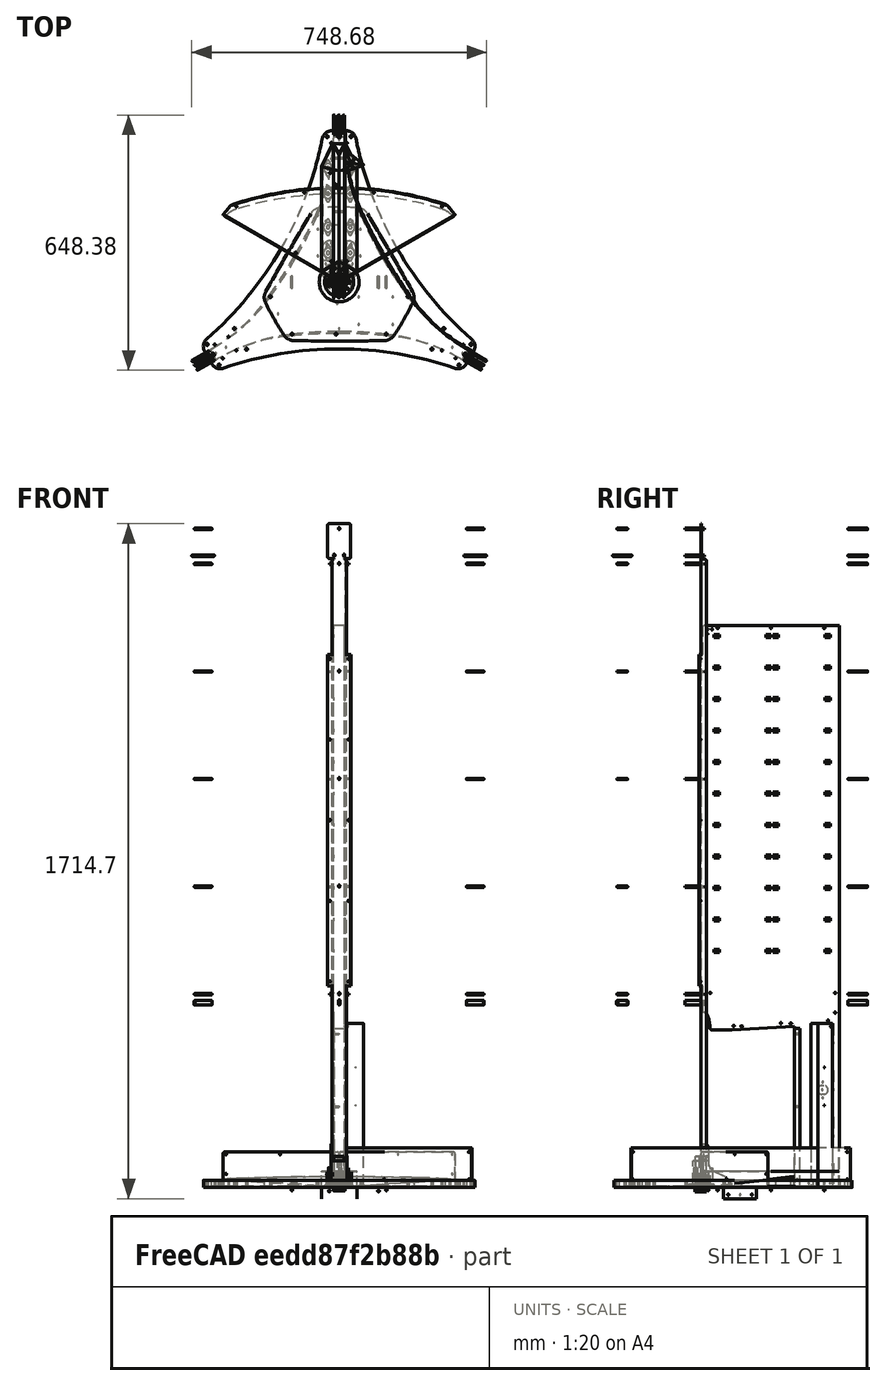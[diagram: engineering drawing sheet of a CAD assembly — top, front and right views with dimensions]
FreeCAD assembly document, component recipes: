
FREECAD ASSEMBLY — COMPONENT RECIPES ("composit_full_size3")

This assembly document has 76 components, labeled P0..P75 below (a component is one placed body or linked part). 73 of them carry a construction recipe — the FreeCAD feature program that regenerates the part from scratch, quoted from this document or its linked companion documents; the rest are supplied as boundary geometry only. No exploded tour is included for this assembly.
NOTE — this tour is split across 3 documents so each fits a 32k-token context. This is document 1: the component sections continue in the remaining 2 documents, each repeating the header above.
COMPONENT P0 — recipe-attached ("tech_sector_pillar_material_0.30ansi", modeled in this document).
Construction recipe (the document's own serialized feature program — sketch geometry with constraints, then the solid features built on it; lengths are millimeters unless a unit is written):

FEATURE [Sketcher::SketchObject] Sketch062
  ArcFitTolerance = 0
  AttachmentSupport = -> [XY_Plane036]
  FullyConstrained = true
  MakeInternals = false
  MapMode = 5
  expr: Constraints[3] = <<Properties>>.endface_width / 2 + 0.5 mm
  sketch-geometry (7):
    g0: LineSegment StartX=61.9452 StartY=297.209 StartZ=0 EndX=15 EndY=280 EndZ=0
    g1: LineSegment StartX=15 StartY=280 StartZ=0 EndX=15 EndY=335 EndZ=0
    g2: LineSegment StartX=15 StartY=335 StartZ=0 EndX=62.031 EndY=297.743 EndZ=0
    g3: LineSegment [constr] StartX=61.9452 StartY=297.209 StartZ=0 EndX=62.4647 EndY=297.399 EndZ=0
    g4: LineSegment [constr] StartX=62.4647 StartY=297.399 StartZ=0 EndX=62.031 EndY=297.743 EndZ=0
    g5: LineSegment [constr] StartX=61.9452 StartY=297.209 StartZ=0 EndX=61.8385 EndY=297.5 EndZ=0
    g6: LineSegment [constr] StartX=61.8385 StartY=297.5 StartZ=0 EndX=62.031 EndY=297.743 EndZ=0
  constraints (20):
    c: Coincident(g0,g1)
    c: Vertical(g1)
    c: Coincident(g1,g2)
    c: DistanceX(g1) = 15
    c: Distance(g1) = 55
    c: Distance(g2) = 60
    c: Distance(g0) = 50
    c: Coincident(g3,g0)
    c: Coincident(g4,g3)
    c: Coincident(g4,g2)
    c: Parallel(g0,g3)
    c: Parallel(g4,g2)
    c: Equal(g3,g4)
    c: Coincident(g0,g5)
    c: Coincident(g5,g6)
    c: Coincident(g6,g2)
    c: Perpendicular(g3,g5)
    c: Perpendicular(g4,g6)
    c: Distance(g5) = 0.31
    c: DistanceY(g1) = 335
FEATURE [PartDesign::FeaturePython] BaseBend020  # WARN: FeaturePython — macro-defined, semantics opaque (R4)
  BendSide = 0
  BendSketch = -> Sketch062
  MidPlane = false
  Reverse = false
  Suppressed = false
  length = 413
  radius = 0.1
  thickness = 0.3
  expr: radius = composit_properties#<<Properties>>.bend_r
  expr: thickness = composit_properties#<<Properties>>.al_thickness
FEATURE [PartDesign::FeaturePython] Bend009  # WARN: FeaturePython — macro-defined, semantics opaque (R4)
  AutoMiter = true
  BaseFeature = -> BaseBend020
  BendType = 0
  LengthList = [15]
  LengthSpec = 0
  NonperforationMaxLength = 5
  Perforate = false
  PerforationAngle = 0
  PerforationInitialLength = 5
  PerforationMaxLength = 5
  ReliefFactor = 0.7
  Suppressed = false
  UseReliefFactor = false
  angle = 90
  baseObject = -> BaseBend020 [Edge17,Edge4,Edge33,Edge32,Edge16,Edge3]
  bendAList = [90]
  extend1 = 0
  extend2 = 0
  gap1 = 0
  gap2 = 0
  invert = true
  kfactor = 0.5
  length = 15
  maxExtendDist = 5
  minGap = 0.1
  minReliefGap = 1
  miterangle1 = 0
  miterangle2 = 0
  offset = 0
  radius = 0.1
  reliefType = 0
  reliefd = 1
  reliefw = 0.8
  sketchflip = false
  sketchinvert = false
  unfold = false
  expr: radius = BaseBend020.radius
FEATURE [Sketcher::SketchObject] Sketch075
  ArcFitTolerance = 0
  AttachmentSupport = -> [XY_Plane036]
  ExternalGeometry = -> [Sketch062]
  FullyConstrained = true
  MakeInternals = false
  MapMode = 5
  expr: Constraints[34] = <<Properties>>.rivet_d
  sketch-geometry (14):
    g0: LineSegment [constr] StartX=15 StartY=280 StartZ=0 EndX=62.4647 EndY=297.399 EndZ=0
    g1: LineSegment [constr] StartX=62.4647 StartY=297.399 StartZ=0 EndX=15 EndY=335 EndZ=0
    g2: LineSegment [constr] StartX=15 StartY=280 StartZ=0 EndX=30.7162 EndY=302.5 EndZ=0
    g3: LineSegment [constr] StartX=30.7162 StartY=302.5 StartZ=0 EndX=15 EndY=335 EndZ=0
    g4: LineSegment [constr] StartX=30.7162 StartY=302.5 StartZ=0 EndX=62.4647 EndY=297.399 EndZ=0
    g5: LineSegment [constr] StartX=15 StartY=302.5 StartZ=0 EndX=30.7162 EndY=302.5 EndZ=0
    g6: LineSegment [constr] StartX=30.7162 StartY=302.5 StartZ=0 EndX=36.1253 EndY=287.744 EndZ=0
    g7: LineSegment [constr] StartX=30.7162 StartY=302.5 StartZ=0 EndX=40.4751 EndY=314.819 EndZ=0
    g8: Circle CenterX=34.4044 CenterY=292.439 CenterZ=0 NormalX=0 NormalY=0 NormalZ=1 AngleXU=0 Radius=1.7
    g9: Circle CenterX=36.2097 CenterY=309.435 CenterZ=0 NormalX=0 NormalY=0 NormalZ=1 AngleXU=0 Radius=1.7
    g10: Circle CenterX=20.588 CenterY=302.5 CenterZ=0 NormalX=0 NormalY=0 NormalZ=1 AngleXU=0 Radius=1.7
    g11: LineSegment [constr] StartX=20.588 StartY=302.5 StartZ=0 EndX=36.2097 EndY=309.435 EndZ=0
    g12: LineSegment [constr] StartX=36.2097 StartY=309.435 StartZ=0 EndX=34.4044 EndY=292.439 EndZ=0
    g13: LineSegment [constr] StartX=34.4044 StartY=292.439 StartZ=0 EndX=20.588 EndY=302.5 EndZ=0
  constraints (36):
    c: Coincident(g-4,g0)
    c: Coincident(g0,g1)
    c: Coincident(g1,g-3)
    c: PointOnObject(g-4,g0)
    c: PointOnObject(g-3,g1)
    c: Coincident(g0,g2)
    c: Coincident(g2,g3)
    c: Coincident(g2,g4)
    c: Coincident(g4,g0)
    c: Coincident(g3,g1)
    c: Coincident(g5,g2)
    c: Horizontal(g5)
    c: Coincident(g5,g6)
    c: PointOnObject(g6,g0)
    c: Perpendicular(g0,g6)
    c: Vertical(g5,g0)
    c: Equal(g6,g5)
    c: Coincident(g7,g2)
    c: PointOnObject(g7,g1)
    c: Perpendicular(g1,g7)
    c: Equal(g6,g7)
    c: PointOnObject(g8,g6)
    c: PointOnObject(g9,g7)
    c: PointOnObject(g10,g5)
    c: Coincident(g11,g10)
    c: Coincident(g11,g9)
    c: Coincident(g11,g12)
    c: Coincident(g12,g8)
    c: Coincident(g12,g13)
    c: Coincident(g13,g11)
    c: Equal(g13,g11)
    c: Equal(g11,g12)
    c: Equal(g8,g10)
    c: Equal(g8,g9)
    c: Diameter(g8) = 3.4
    c: Distance(g8,g6) = 5
FEATURE [PartDesign::Pocket] Pocket035
  BaseFeature = -> Bend009
  Direction = (0,0,-1)
  Length = 5
  Length2 = 5
  Midplane = true
  Profile = -> Sketch075
  ReferenceAxis = -> Sketch075 [N_Axis]
  Suppressed = false
  Type = 1
FEATURE [PartDesign::Plane] DatumPlane001
  AttachmentOffset = pos=(0,0,0) rot=(0,1,0;1.5708rad)
  AttachmentSupport = -> [Sketch062]
  Length = 362.992
  MapMode = 7
  Placement = pos=(15,335,0) rot=(-0.89718,0.312304,0.312304;4.6041rad)
  ResizeMode = 0
  Width = 509.896
FEATURE [Sketcher::SketchObject] Sketch077
  ArcFitTolerance = 0
  AttachmentSupport = -> [DatumPlane001]
  FullyConstrained = true
  MakeInternals = false
  MapMode = 5
  Placement = pos=(15,335,0) rot=(0.89718,-0.312304,-0.312304;1.67908rad)
  expr: Constraints[1] = <<Properties>>.rivet_d
  expr: Constraints[3] = BaseBend020.length
  sketch-geometry (4):
    g0: Circle CenterX=10 CenterY=7 CenterZ=0 NormalX=0 NormalY=0 NormalZ=1 AngleXU=0 Radius=1.7
    g1: Circle CenterX=10 CenterY=406 CenterZ=0 NormalX=0 NormalY=0 NormalZ=1 AngleXU=0 Radius=1.7
    g2: GeomPoint [constr] X=0 Y=413 Z=0
    g3: LineSegment [constr] StartX=0 StartY=206.5 StartZ=0 EndX=10 EndY=206.5 EndZ=0
  constraints (10):
    c: Equal(g0,g1)
    c: Diameter(g0) = 3.4
    c: PointOnObject(g2,g-2)
    c: DistanceY(g2) = 413
    c: DistanceX(g0) = 10
    c: DistanceY(g0) = 7
    c: Vertical(g1,g0)
    c: Horizontal(g3)
    c: Symmetric(g-1,g2,g3)
    c: Symmetric(g1,g0,g3)
FEATURE [PartDesign::Hole] Hole006
  BaseFeature = -> Pocket035
  CustomThreadClearance = 0
  Depth = 1
  DepthType = 0
  Diameter = 3.4
  DrillForDepth = false
  DrillPoint = 1
  DrillPointAngle = 118
  HoleCutCountersinkAngle = 90
  HoleCutCustomValues = false
  HoleCutDepth = 0
  HoleCutDiameter = 6.1
  HoleCutType = 0
  ModelThread = false
  Profile = -> Sketch077
  Reversed = true
  Suppressed = false
  Tapered = false
  TaperedAngle = 90
  ThreadClass = 0
  ThreadDepth = 1
  ThreadDepthType = 0
  ThreadDirection = 0
  ThreadFit = 0
  ThreadSize = 0
  ThreadType = 0
  Threaded = false
  UseCustomThreadClearance = false
  expr: Diameter = <<Properties>>.rivet_d
FEATURE [Sketcher::SketchObject] Sketch078  label="pillar_magnet_fix"
  ArcFitTolerance = 0
  AttachmentOffset = pos=(0,0,0) rot=(0,1,0;1.5708rad)
  AttachmentSupport = -> [Sketch062]
  FullyConstrained = true
  MakeInternals = false
  MapMode = 7
  Placement = pos=(15,280,0) rot=(0.57735,0.57735,0.57735;2.0944rad)
  expr: Constraints[11] = <<Properties>>.rivet_d
  sketch-geometry (8):
    g0: ArcOfCircle CenterX=32.5 CenterY=244.5 CenterZ=0 NormalX=0 NormalY=0 NormalZ=1 AngleXU=0 Radius=11 StartAngle=4.71239 EndAngle=7.85398
    g1: ArcOfCircle CenterX=27.5 CenterY=244.5 CenterZ=0 NormalX=0 NormalY=0 NormalZ=1 AngleXU=0 Radius=11 StartAngle=1.5708 EndAngle=4.71239
    g2: LineSegment StartX=32.5 StartY=255.5 StartZ=0 EndX=27.5 EndY=255.5 EndZ=0
    g3: LineSegment StartX=27.5 StartY=233.5 StartZ=0 EndX=32.5 EndY=233.5 EndZ=0
    g4: Circle CenterX=30 CenterY=224.5 CenterZ=0 NormalX=0 NormalY=0 NormalZ=1 AngleXU=0 Radius=1.7
    g5: Circle CenterX=30 CenterY=264.5 CenterZ=0 NormalX=0 NormalY=0 NormalZ=1 AngleXU=0 Radius=1.7
    g6: LineSegment [constr] StartX=27.5 StartY=244.5 StartZ=0 EndX=30 EndY=244.5 EndZ=0
    g7: LineSegment [constr] StartX=32.5 StartY=244.5 StartZ=0 EndX=30 EndY=244.5 EndZ=0
  constraints (20):
    c: Tangent(g0,g2) = -1.5708
    c: Tangent(g2,g1) = -1.5708
    c: Tangent(g1,g3) = -1.5708
    c: Tangent(g3,g0) = -1.5708
    c: Equal(g0,g1)
    c: Coincident(g6,g1)
    c: Coincident(g7,g0)
    c: Coincident(g7,g6)
    c: Equal(g6,g7)
    c: Symmetric(g4,g5,g6)
    c: Equal(g4,g5)
    c: Diameter(g4) = 3.4
    c: Parallel(g6,g7)
    c: Distance(g1,g0) = 5
    c: Diameter(g0) = 22
    c: Horizontal(g1,g0)
    c: DistanceY(g4,g5) = 40
    c: DistanceY(g6) = 244.5  'height'
    c: DistanceX(g6) = 30
    c: Vertical(g4,g5)
FEATURE [PartDesign::Pocket] Pocket037
  BaseFeature = -> Hole006
  Direction = (-1,2e-16,0)
  Length = 5
  Length2 = 5
  Midplane = true
  Profile = -> Sketch078
  ReferenceAxis = -> Sketch078 [N_Axis]
  Suppressed = false
  Type = 0
FEATURE [Sketcher::SketchObject] Sketch079
  ArcFitTolerance = 0
  AttachmentSupport = -> [DatumPlane001]
  FullyConstrained = true
  MakeInternals = false
  MapMode = 5
  Placement = pos=(15,335,0) rot=(0.89718,-0.312304,-0.312304;1.67908rad)
  expr: Constraints[3] = BaseBend020.length - 111.35 mm
  sketch-geometry (2):
    g0: Circle CenterX=35 CenterY=301.65 CenterZ=0 NormalX=0 NormalY=0 NormalZ=1 AngleXU=0 Radius=1.25
    g1: Circle CenterX=35 CenterY=205.65 CenterZ=0 NormalX=0 NormalY=0 NormalZ=1 AngleXU=0 Radius=1.25
  constraints (6):
    c: Vertical(g1,g0)
    c: DistanceY(g1,g0) = 96
    c: DistanceX(g1) = 35
    c: DistanceY(g0) = 301.65
    c: Equal(g1,g0)
    c: Diameter(g1) = 2.5
FEATURE [PartDesign::Hole] Hole009
  BaseFeature = -> Pocket037
  CustomThreadClearance = 0
  Depth = 25
  DepthType = 0
  Diameter = 2.5
  DrillForDepth = false
  DrillPoint = 1
  DrillPointAngle = 118
  HoleCutCountersinkAngle = 90
  HoleCutCustomValues = false
  HoleCutDepth = 0
  HoleCutDiameter = 6.1
  HoleCutType = 0
  ModelThread = false
  Profile = -> Sketch079
  Reversed = true
  Suppressed = false
  Tapered = false
  TaperedAngle = 90
  ThreadClass = 0
  ThreadDepth = 25
  ThreadDepthType = 0
  ThreadDirection = 0
  ThreadFit = 0
  ThreadSize = 0
  ThreadType = 0
  Threaded = false
  UseCustomThreadClearance = false
FEATURE [PartDesign::Body] Body073  label="tech_sector_pillar_material_0.30ansi"
  AllowCompound = false
  Group = -> [Sketch062,BaseBend020,Bend009,Sketch075,Pocket035,DatumPlane001,Sketch077,Hole006,Sketch078,Pocket037,Sketch079,Hole009]
  Origin = -> Origin036
  Placement = pos=(0,0,3) rot=(0,0,1;0rad)
  Tip = -> Hole009
COMPONENT P1 — recipe-attached ("tech_sector_hor", modeled in this document).
Construction recipe (the document's own serialized feature program — sketch geometry with constraints, then the solid features built on it; lengths are millimeters unless a unit is written):

FEATURE [PartDesign::SubShapeBinder] Binder038
  BindCopyOnChange = 0
  BindMode = 0
  ClaimChildren = true
  Context = -> Body074 [Binder038.]
  Fuse = false
  MakeFace = true
  OffsetFill = false
  OffsetIntersection = false
  OffsetJoinType = 0
  OffsetOpenResult = false
  PartialLoad = false
  Relative = true
  Support = -> [Compound037]
  _Version = 2
FEATURE [PartDesign::Pad] Pad008
  Direction = (0,0,1)
  Length = 3
  Length2 = 10
  Profile = -> Binder038
  Suppressed = false
  Type = 0
FEATURE [PartDesign::SubShapeBinder] Binder044
  BindCopyOnChange = 0
  BindMode = 0
  ClaimChildren = false
  Context = -> Body074 [Binder044.]
  Fuse = false
  MakeFace = true
  OffsetFill = false
  OffsetIntersection = false
  OffsetJoinType = 0
  OffsetOpenResult = false
  PartialLoad = false
  Relative = true
  Support = -> [Body073[Pocket035.Sketch075.]]
  _Version = 2
FEATURE [PartDesign::Pocket] Pocket036
  BaseFeature = -> Pad008
  Direction = (0,0,-1)
  Length = 5
  Length2 = 5
  Midplane = true
  Profile = -> Binder044
  Suppressed = false
  Type = 1
FEATURE [PartDesign::Plane] DatumPlane
  AttachmentOffset = pos=(0,0,0) rot=(0,1,0;0.523599rad)
  AttachmentSupport = -> [XZ_Plane037]
  Length = 552.693
  MapMode = 5
  Placement = pos=(0,0,0) rot=(0.935113,0.250563,0.250563;1.63783rad)
  ResizeMode = 0
  Width = 82.2624
FEATURE [PartDesign::Mirrored] Mirrored003
  BaseFeature = -> Pocket036
  MirrorPlane = -> DatumPlane
  Originals = -> [Pocket036]
  Suppressed = false
  TransformMode = 0
FEATURE [Sketcher::SketchObject] Sketch083
  ArcFitTolerance = 0
  AttachmentSupport = -> [XY_Plane037]
  ExternalGeometry = -> [Binder038]
  FullyConstrained = true
  MakeInternals = false
  MapMode = 5
  expr: Constraints[4] = <<Properties>>.rivet_d
  sketch-geometry (2):
    g0: LineSegment [constr] StartX=212.95 StartY=122.947 StartZ=0 EndX=201.691 EndY=116.447 EndZ=0
    g1: Circle CenterX=201.691 CenterY=116.447 CenterZ=0 NormalX=0 NormalY=0 NormalZ=1 AngleXU=0 Radius=1.7
  constraints (5):
    c: Coincident(g0,g-3)
    c: Perpendicular(g-3,g0)
    c: Distance(g0) = 13
    c: Coincident(g1,g0)
    c: Diameter(g1) = 3.4
FEATURE [PartDesign::Hole] Hole011
  BaseFeature = -> Mirrored003
  CustomThreadClearance = 0
  Depth = 25
  DepthType = 0
  Diameter = 3.4
  DrillForDepth = false
  DrillPoint = 1
  DrillPointAngle = 118
  HoleCutCountersinkAngle = 90
  HoleCutCustomValues = false
  HoleCutDepth = 0
  HoleCutDiameter = 6.1
  HoleCutType = 0
  ModelThread = false
  Profile = -> Sketch083
  Reversed = true
  Suppressed = false
  Tapered = false
  TaperedAngle = 90
  ThreadClass = 0
  ThreadDepth = 25
  ThreadDepthType = 0
  ThreadDirection = 0
  ThreadFit = 0
  ThreadSize = 0
  ThreadType = 0
  Threaded = false
  UseCustomThreadClearance = false
  expr: Diameter = <<Properties>>.rivet_d
FEATURE [PartDesign::Body] Body074  label="tech_sector_hor"
  AllowCompound = false
  Group = -> [Binder038,Pad008,Binder044,Pocket036,DatumPlane,Mirrored003,Sketch083,Hole011]
  Origin = -> Origin037
  Tip = -> Hole011
COMPONENT P2 — recipe-attached ("tech_sector_plexiglass_material_0.30ansi", modeled in this document).
Construction recipe (the document's own serialized feature program — sketch geometry with constraints, then the solid features built on it; lengths are millimeters unless a unit is written):

FEATURE [PartDesign::SubShapeBinder] Binder045
  BindCopyOnChange = 0
  BindMode = 0
  ClaimChildren = false
  Context = -> Body077 [Binder045.]
  Fuse = false
  MakeFace = true
  OffsetFill = false
  OffsetIntersection = false
  OffsetJoinType = 0
  OffsetOpenResult = false
  PartialLoad = false
  Relative = true
  Support = -> [Body074[Binder038.Compound037.Sketch063.]]
  _Version = 2
FEATURE [Sketcher::SketchObject] Sketch076
  ArcFitTolerance = 0
  AttachmentSupport = -> [XY_Plane041]
  ExternalGeometry = -> [Binder045]
  FullyConstrained = true
  MakeInternals = false
  MapMode = 5
  sketch-geometry (5):
    g0: LineSegment StartX=15 StartY=335 StartZ=0 EndX=62.031 EndY=297.743 EndZ=0
    g1: ArcOfCircle CenterX=-320.353 CenterY=-184.956 CenterZ=0 NormalX=0 NormalY=0 NormalZ=1 AngleXU=0 Radius=615.805 StartAngle=0.146355 EndAngle=0.900842
    g2: LineSegment StartX=288.868 StartY=-95.1511 StartZ=0 EndX=297.619 EndY=-154.51 EndZ=0
    g3: LineSegment [constr] StartX=-320.353 StartY=-184.956 StartZ=0 EndX=212.95 EndY=122.947 EndZ=0
    g4: LineSegment [constr] StartX=62.031 StartY=297.743 StartZ=0 EndX=288.868 EndY=-95.1511 EndZ=0
  constraints (12):
    c: Coincident(g0,g-4)
    c: Coincident(g1,g-4)
    c: Coincident(g1,g0)
    c: Tangent(g2,g1) = 1.5708
    c: Coincident(g3,g1)
    c: Coincident(g3,g-4)
    c: Vertical(g0,g-5)
    c: Equal(g0,g2)
    c: PointOnObject(g-3,g0)
    c: Coincident(g4,g0)
    c: Coincident(g4,g1)
    c: Perpendicular(g3,g4)
FEATURE [PartDesign::FeaturePython] BaseBend021  # WARN: FeaturePython — macro-defined, semantics opaque (R4)
  BendSide = 1
  BendSketch = -> Sketch076
  MidPlane = false
  Reverse = false
  Suppressed = false
  length = 419
  radius = 1
  thickness = 1.5
  expr: length = BaseBend020.length + composit_properties#<<Properties>>.thickness * 2
FEATURE [PartDesign::Fillet] Fillet
  Base = -> BaseBend021 [Edge10,Edge8,Edge25,Edge23]
  BaseFeature = -> BaseBend021
  Radius = 3
  SupportTransform = false
  Suppressed = false
  UseAllEdges = false
FEATURE [PartDesign::SubShapeBinder] Binder046
  BindCopyOnChange = 0
  BindMode = 0
  ClaimChildren = false
  Context = -> Body077 [Binder046.]
  Fuse = false
  MakeFace = true
  OffsetFill = false
  OffsetIntersection = false
  OffsetJoinType = 0
  OffsetOpenResult = false
  PartialLoad = false
  Relative = true
  Support = -> [Body073[Hole006.Sketch077.]]
  _Version = 2
FEATURE [PartDesign::SubShapeBinder] Binder047
  BindCopyOnChange = 0
  BindMode = 0
  ClaimChildren = true
  Context = -> Body077 [Binder047.]
  Fuse = false
  MakeFace = true
  OffsetFill = false
  OffsetIntersection = false
  OffsetJoinType = 0
  OffsetOpenResult = false
  PartialLoad = false
  Relative = true
  Support = -> [Body073[Sketch079.]]
  _Version = 2
FEATURE [PartDesign::Plane] DatumPlane002
  AttachmentOffset = pos=(0,0,0) rot=(0,1,0;0.523599rad)
  AttachmentSupport = -> [XZ_Plane041]
  Length = 622.679
  MapMode = 5
  Placement = pos=(0,0,0) rot=(0.935113,0.250563,0.250563;1.63783rad)
  ResizeMode = 0
  Width = 540.655
FEATURE [Sketcher::SketchObject] Sketch084
  ArcFitTolerance = 0
  AttachmentSupport = -> [Binder046]
  ExternalGeometry = -> [Binder046]
  FullyConstrained = false
  MakeInternals = false
  MapMode = 5
  Placement = pos=(168.839,213.132,5.5e-14) rot=(0.239007,0.686613,0.686613;2.67238rad)
  sketch-geometry (3):
    g0: Circle CenterX=186.261 CenterY=409.25 CenterZ=0 NormalX=0 NormalY=0 NormalZ=1 AngleXU=0 Radius=1.69397
    g1: Circle CenterX=186.261 CenterY=9.75 CenterZ=0 NormalX=0 NormalY=0 NormalZ=1 AngleXU=0 Radius=1.72481
    g2: GeomPoint [constr] X=186.261 Y=209.5 Z=0
  constraints (4):
    c: Symmetric(g-4,g-3,g2)
    c: Symmetric(g1,g0,g2)
    c: Vertical(g-3,g0)
    c: DistanceY(g-3,g0) = 0.25
FEATURE [PartDesign::Hole] Hole007
  BaseFeature = -> Fillet
  CustomThreadClearance = 0
  Depth = 25
  DepthType = 0
  Diameter = 3.4
  DrillForDepth = false
  DrillPoint = 1
  DrillPointAngle = 118
  HoleCutCountersinkAngle = 90
  HoleCutCustomValues = false
  HoleCutDepth = 0
  HoleCutDiameter = 6.1
  HoleCutType = 0
  ModelThread = false
  Profile = -> Sketch084
  Reversed = true
  Suppressed = false
  Tapered = false
  TaperedAngle = 90
  ThreadClass = 0
  ThreadDepth = 25
  ThreadDepthType = 0
  ThreadDirection = 0
  ThreadFit = 0
  ThreadSize = 0
  ThreadType = 0
  Threaded = false
  UseCustomThreadClearance = false
  expr: Diameter = <<Properties>>.rivet_d
FEATURE [PartDesign::Hole] Hole008
  BaseFeature = -> Hole007
  CustomThreadClearance = 0
  Depth = 25
  DepthType = 0
  Diameter = 3.4
  DrillForDepth = false
  DrillPoint = 1
  DrillPointAngle = 118
  HoleCutCountersinkAngle = 90
  HoleCutCustomValues = false
  HoleCutDepth = 0
  HoleCutDiameter = 6.1
  HoleCutType = 0
  ModelThread = false
  Profile = -> Binder047
  Reversed = true
  Suppressed = false
  Tapered = false
  TaperedAngle = 90
  ThreadClass = 0
  ThreadDepth = 25
  ThreadDepthType = 0
  ThreadDirection = 0
  ThreadFit = 0
  ThreadSize = 0
  ThreadType = 0
  Threaded = false
  UseCustomThreadClearance = false
  expr: Diameter = <<Properties>>.rivet_d
FEATURE [PartDesign::Mirrored] Mirrored004
  BaseFeature = -> Hole008
  MirrorPlane = -> DatumPlane002
  Originals = -> [Hole007,Hole008]
  Suppressed = false
  TransformMode = 0
FEATURE [PartDesign::Body] Body077  label="tech_sector_plexiglass_material_0.30ansi"
  AllowCompound = false
  Group = -> [Binder045,Sketch076,BaseBend021,Fillet,Binder046,Hole007,Binder047,Hole008,DatumPlane002,Mirrored004,Sketch084]
  Origin = -> Origin041
  Tip = -> Mirrored004
COMPONENT P3 — recipe-attached ("basement_amplifier_material_0.30ansi", modeled in this document).
Construction recipe (the document's own serialized feature program — sketch geometry with constraints, then the solid features built on it; lengths are millimeters unless a unit is written):

FEATURE [Sketcher::SketchObject] Sketch121
  ArcFitTolerance = 0
  AttachmentSupport = -> [XZ_Plane054]
  FullyConstrained = true
  MakeInternals = false
  MapMode = 5
  Placement = pos=(0,0,0) rot=(1,0,0;1.5708rad)
  sketch-geometry (5):
    g0: LineSegment StartX=-18 StartY=15 StartZ=0 EndX=-18 EndY=0 EndZ=0
    g1: LineSegment StartX=-18 StartY=0 StartZ=0 EndX=18 EndY=0 EndZ=0
    g2: LineSegment StartX=18 StartY=0 StartZ=0 EndX=18 EndY=15 EndZ=0
    g3: LineSegment [constr] StartX=18 StartY=15 StartZ=0 EndX=-18 EndY=15 EndZ=0
    g4: GeomPoint [constr] X=0 Y=7.5 Z=0
  constraints (13):
    c: Coincident(g0,g1)
    c: Coincident(g1,g2)
    c: Coincident(g2,g3)
    c: Coincident(g3,g0)
    c: Horizontal(g1)
    c: Horizontal(g3)
    c: Vertical(g0)
    c: Vertical(g2)
    c: Symmetric(g1,g0,g4)
    c: PointOnObject(g4,g-2)
    c: PointOnObject(g1,g-1)
    c: DistanceY(g2,g2) = 15  'height'
    c: DistanceX(g1,g1) = 36  'width'
FEATURE [PartDesign::FeaturePython] BaseBend030  # WARN: FeaturePython — macro-defined, semantics opaque (R4)
  BendSide = 1
  BendSketch = -> Sketch121
  MidPlane = true
  Reverse = false
  Suppressed = false
  length = 245
  radius = 2
  thickness = 2
FEATURE [Sketcher::SketchObject] Sketch122
  ArcFitTolerance = 0
  AttachmentSupport = -> [YZ_Plane054]
  FullyConstrained = true
  MakeInternals = false
  MapMode = 5
  Placement = pos=(0,0,0) rot=(0.57735,0.57735,0.57735;2.0944rad)
  expr: Constraints[10] = Sketch121.Constraints.height
  expr: Constraints[12] = BaseBend030.length / 2
  expr: Constraints[9] = BaseBend030.thickness + BaseBend030.radius
  sketch-geometry (14):
    g0: ArcOfCircle CenterX=117.5 CenterY=4 CenterZ=0 NormalX=0 NormalY=0 NormalZ=1 AngleXU=0 Radius=5 StartAngle=1e-16 EndAngle=0.785398
    g1: LineSegment StartX=121.036 StartY=7.53553 StartZ=0 EndX=115.036 EndY=13.5355 EndZ=0
    g2: ArcOfCircle CenterX=111.5 CenterY=10 CenterZ=0 NormalX=0 NormalY=0 NormalZ=1 AngleXU=0 Radius=5 StartAngle=0.785398 EndAngle=1.5708
    g3: LineSegment StartX=111.5 StartY=15 StartZ=0 EndX=-111.5 EndY=15 EndZ=0
    g4: LineSegment StartX=122.5 StartY=4 StartZ=0 EndX=122.5 EndY=0 EndZ=0
    g5: LineSegment StartX=122.5 StartY=0 StartZ=0 EndX=-122.5 EndY=0 EndZ=0
    g6: LineSegment StartX=-122.5 StartY=0 StartZ=0 EndX=-122.5 EndY=4 EndZ=0
    g7: LineSegment StartX=-121.036 StartY=7.53553 StartZ=0 EndX=-115.036 EndY=13.5355 EndZ=0
    g8: ArcOfCircle CenterX=-111.5 CenterY=10 CenterZ=0 NormalX=0 NormalY=0 NormalZ=1 AngleXU=0 Radius=5 StartAngle=1.5708 EndAngle=2.35619
    g9: GeomPoint [constr] X=-113.571 Y=15 Z=0
    g10: ArcOfCircle CenterX=-117.5 CenterY=4 CenterZ=0 NormalX=0 NormalY=0 NormalZ=1 AngleXU=0 Radius=5 StartAngle=2.35619 EndAngle=3.14159
    g11: GeomPoint [constr] X=-122.5 Y=6.07107 Z=0
    g12: GeomPoint [constr] X=113.571 Y=15 Z=0
    g13: GeomPoint [constr] X=122.5 Y=6.07107 Z=0
  constraints (32):
    c: Tangent(g1,g0) = -1.5708
    c: Angle(g1) = 2.35619
    c: Tangent(g2,g1) = -1.5708
    c: Horizontal(g3)
    c: Tangent(g3,g2) = -1.5708
    c: Equal(g0,g2)
    c: Tangent(g0,g4) = 1.5708
    c: Coincident(g4,g5)
    c: Horizontal(g5)
    c: DistanceY(g0) = 4
    c: DistanceY(g9) = 15
    c: Vertical(g4)
    c: DistanceX(g4) = 122.5
    c: Radius(g0) = 5
    c: Coincident(g5,g6)
    c: Tangent(g3,g8) = -1.5708
    c: Tangent(g7,g8) = 1.5708
    c: PointOnObject(g11,g6)
    c: PointOnObject(g11,g7)
    c: Tangent(g6,g10) = 1.5708
    c: Tangent(g7,g10) = 1.5708
    c: Vertical(g6)
    c: Equal(g10,g8)
    c: Equal(g8,g2)
    c: PointOnObject(g13,g4)
    c: PointOnObject(g13,g1)
    c: PointOnObject(g12,g1)
    c: Symmetric(g13,g11,g-2)
    c: Symmetric(g9,g12,g-2)
    c: PointOnObject(g9,g3)
    c: PointOnObject(g9,g7)
    c: PointOnObject(g-1,g5)
FEATURE [Part::FeaturePython] WireFilter003  # WARN: FeaturePython — macro-defined, semantics opaque (R4)
  AttacherType = Attacher::AttachEngine3D
  ClaimChildren = true
  ColorKeyCount = 8
  Colorize = true
  FaceMaker = 5
  FixNormal = false
  FollowSource = true
  InvertedFaceScale = 5
  MaxWires = 25
  Normal = (1,0,0)
  OffsetFill = false
  OffsetIntersection = false
  OffsetJoin = 0
  OffsetOpenResult = false
  Scale = (1,1,1)
  SelectEdges = false
  Source = -> Sketch122
  UniformScale = 1
  UseDefault = false
  UseSelected = true
  UseSelectedEdges = false
  Version = 0.2022.02.09
  WireOrder = [1]
FEATURE [PartDesign::Pocket] Pocket066
  BaseFeature = -> BaseBend030
  Direction = (-1,0,0)
  Length = 5
  Length2 = 5
  Midplane = true
  Profile = -> WireFilter003
  Suppressed = false
  Type = 1
FEATURE [Sketcher::SketchObject] Sketch123
  ArcFitTolerance = 0
  AttachmentSupport = -> [XY_Plane054]
  FullyConstrained = true
  MakeInternals = false
  MapMode = 5
  expr: Constraints[1] = -BaseBend030.length / 2
  expr: Constraints[32] = BaseBend030.length - 14 mm
  sketch-geometry (15):
    g0: GeomPoint [constr] X=0 Y=-122.5 Z=0
    g1: Circle CenterX=0 CenterY=92.5 CenterZ=0 NormalX=0 NormalY=0 NormalZ=1 AngleXU=0 Radius=2.5
    g2: LineSegment [constr] StartX=9 StartY=115.5 StartZ=0 EndX=-9 EndY=115.5 EndZ=0
    g3: LineSegment [constr] StartX=-9 StartY=115.5 StartZ=0 EndX=-9 EndY=0 EndZ=0
    g4: LineSegment [constr] StartX=-9 StartY=0 StartZ=0 EndX=-9 EndY=-115.5 EndZ=0
    g5: LineSegment [constr] StartX=-9 StartY=-115.5 StartZ=0 EndX=9 EndY=-115.5 EndZ=0
    g6: LineSegment [constr] StartX=9 StartY=-115.5 StartZ=0 EndX=9 EndY=0 EndZ=0
    g7: LineSegment [constr] StartX=9 StartY=0 StartZ=0 EndX=9 EndY=115.5 EndZ=0
    g8: Circle CenterX=-9 CenterY=0 CenterZ=0 NormalX=0 NormalY=0 NormalZ=1 AngleXU=0 Radius=2.5
    g9: Circle CenterX=9 CenterY=0 CenterZ=0 NormalX=0 NormalY=0 NormalZ=1 AngleXU=0 Radius=2.5
    g10: Circle CenterX=-9 CenterY=115.5 CenterZ=0 NormalX=0 NormalY=0 NormalZ=1 AngleXU=0 Radius=2.5
    g11: Circle CenterX=9 CenterY=115.5 CenterZ=0 NormalX=0 NormalY=0 NormalZ=1 AngleXU=0 Radius=2.5
    g12: Circle CenterX=-9 CenterY=-115.5 CenterZ=0 NormalX=0 NormalY=0 NormalZ=1 AngleXU=0 Radius=2.5
    g13: Circle CenterX=9 CenterY=-115.5 CenterZ=0 NormalX=0 NormalY=0 NormalZ=1 AngleXU=0 Radius=2.5
    g14: Circle CenterX=0 CenterY=-92.5 CenterZ=0 NormalX=0 NormalY=0 NormalZ=1 AngleXU=0 Radius=4
  constraints (36):
    c: PointOnObject(g0,g-2)
    c: DistanceY(g0) = -122.5
    c: PointOnObject(g1,g-2)
    c: DistanceY(g0,g1) = 215
    c: Horizontal(g2)
    c: Coincident(g2,g3)
    c: PointOnObject(g3,g-1)
    c: Vertical(g3)
    c: Coincident(g3,g4)
    c: Vertical(g4)
    c: Coincident(g4,g5)
    c: Horizontal(g5)
    c: Coincident(g5,g6)
    c: PointOnObject(g6,g-1)
    c: Vertical(g6)
    c: Coincident(g6,g7)
    c: Coincident(g7,g2)
    c: Vertical(g7)
    c: Coincident(g8,g3)
    c: Coincident(g9,g6)
    c: Coincident(g10,g2)
    c: Coincident(g11,g2)
    c: Coincident(g12,g4)
    c: Coincident(g13,g5)
    c: Symmetric(g12,g11,g-1)
    c: Equal(g11,g10)
    c: Equal(g11,g1)
    c: Equal(g11,g8)
    c: Equal(g11,g9)
    c: Equal(g11,g12)
    c: Equal(g11,g13)
    c: Diameter(g11) = 5
    c: DistanceY(g12,g10) = 231
    c: DistanceX(g2,g2) = 18
    c: Diameter(g14) = 8
    c: Symmetric(g14,g1,g-1)
FEATURE [PartDesign::Pocket] Pocket067
  BaseFeature = -> Pocket066
  Direction = (0,0,-1)
  Length = 5
  Length2 = 5
  Profile = -> Sketch123
  ReferenceAxis = -> Sketch123 [N_Axis]
  Reversed = true
  Suppressed = false
  Type = 0
FEATURE [PartDesign::Body] Body088  label="basement_amplifier_material_0.30ansi"
  AllowCompound = false
  Group = -> [Sketch121,BaseBend030,Sketch122,WireFilter003,Pocket066,Sketch123,Pocket067]
  Origin = -> Origin054
  Tip = -> Pocket067
COMPONENT P4 — recipe-attached ("door_base_pillar_material_0.45ansi", modeled in this document).
Construction recipe (the document's own serialized feature program — sketch geometry with constraints, then the solid features built on it; lengths are millimeters unless a unit is written):

FEATURE [PartDesign::SubShapeBinder] Binder083
  BindCopyOnChange = 0
  BindMode = 0
  ClaimChildren = true
  Context = -> Body095 [Binder083.]
  Fuse = false
  MakeFace = true
  OffsetFill = false
  OffsetIntersection = false
  OffsetJoinType = 0
  OffsetOpenResult = false
  PartialLoad = false
  Relative = false
  Support = -> [Sketch128]
  _Version = 2
FEATURE [PartDesign::FeaturePython] BaseBend034  label="door_base_pillar_BaseBend"  # WARN: FeaturePython — macro-defined, semantics opaque (R4)
  BendSide = 0
  BendSketch = -> Binder083
  MidPlane = false
  Reverse = false
  Suppressed = false
  length = 1200
  radius = 2
  thickness = 1
FEATURE [PartDesign::SubShapeBinder] Binder092
  BindCopyOnChange = 0
  BindMode = 0
  ClaimChildren = true
  Context = -> Body095 [Binder092.]
  Fuse = false
  MakeFace = true
  OffsetFill = false
  OffsetIntersection = false
  OffsetJoinType = 0
  OffsetOpenResult = false
  PartialLoad = false
  Relative = true
  Support = -> [Sketch141]
  _Version = 2
FEATURE [PartDesign::Pocket] Pocket075
  BaseFeature = -> BaseBend034
  Direction = (0,-1,0)
  Length = 5
  Length2 = 5
  Midplane = true
  Profile = -> Binder092
  Suppressed = false
  Type = 1
FEATURE [Sketcher::SketchObject] Sketch159
  ArcFitTolerance = 0
  AttachmentSupport = -> [BaseBend034]
  FullyConstrained = true
  MakeInternals = false
  MapMode = 5
  Placement = pos=(40.5,0,0) rot=(0.57735,0.57735,0.57735;2.0944rad)
  sketch-geometry (2):
    g0: Circle CenterX=345 CenterY=1094 CenterZ=0 NormalX=0 NormalY=0 NormalZ=1 AngleXU=0 Radius=1.7
    g1: Circle CenterX=345 CenterY=154 CenterZ=0 NormalX=0 NormalY=0 NormalZ=1 AngleXU=0 Radius=1.7
  constraints (6):
    c: DistanceY(g0) = 1094
    c: DistanceY(g1,g0) = 940
    c: Equal(g0,g1)
    c: Diameter(g0) = 3.4
    c: Vertical(g1,g0)
    c: DistanceX(g0) = 345
FEATURE [Sketcher::SketchObject] Sketch160
  ArcFitTolerance = 0
  AttachmentSupport = -> [BaseBend034]
  FullyConstrained = true
  MakeInternals = false
  MapMode = 5
  Placement = pos=(31.1979,356.594,0) rot=(0.998099,-0.043578,-0.043578;1.5727rad)
  sketch-geometry (8):
    g0: Circle CenterX=17.5 CenterY=1094 CenterZ=0 NormalX=0 NormalY=0 NormalZ=1 AngleXU=0 Radius=1.7
    g1: Circle CenterX=33.5 CenterY=1094 CenterZ=0 NormalX=0 NormalY=0 NormalZ=1 AngleXU=0 Radius=1.7
    g2: Circle CenterX=17.5 CenterY=154 CenterZ=0 NormalX=0 NormalY=0 NormalZ=1 AngleXU=0 Radius=1.7
    g3: Circle CenterX=33.5 CenterY=154 CenterZ=0 NormalX=0 NormalY=0 NormalZ=1 AngleXU=0 Radius=1.7
    g4: LineSegment [constr] StartX=17.5 StartY=154 StartZ=0 EndX=33.5 EndY=154 EndZ=0
    g5: LineSegment [constr] StartX=33.5 StartY=154 StartZ=0 EndX=33.5 EndY=1094 EndZ=0
    g6: LineSegment [constr] StartX=33.5 StartY=1094 StartZ=0 EndX=17.5 EndY=1094 EndZ=0
    g7: LineSegment [constr] StartX=17.5 StartY=1094 StartZ=0 EndX=17.5 EndY=154 EndZ=0
  constraints (20):
    c: Equal(g0,g1)
    c: Diameter(g0) = 3.4
    c: Equal(g2,g3)
    c: Equal(g3,g0)
    c: Coincident(g4,g5)
    c: Coincident(g5,g6)
    c: Coincident(g6,g7)
    c: Coincident(g7,g4)
    c: Horizontal(g4)
    c: Horizontal(g6)
    c: Vertical(g5)
    c: Vertical(g7)
    c: Coincident(g4,g2)
    c: Coincident(g5,g1)
    c: Coincident(g4,g3)
    c: Coincident(g6,g0)
    c: DistanceY(g0) = 1094
    c: DistanceY(g7,g7) = 940
    c: DistanceX(g6,g6) = 16
    c: DistanceX(g0) = 17.5
FEATURE [Sketcher::SketchObject] Sketch161
  ArcFitTolerance = 0
  AttachmentSupport = -> [BaseBend034]
  FullyConstrained = true
  MakeInternals = false
  MapMode = 5
  Placement = pos=(40.5,0,0) rot=(0.57735,0.57735,0.57735;2.0944rad)
  sketch-geometry (8):
    g0: Circle CenterX=343.262 CenterY=363.2 CenterZ=0 NormalX=0 NormalY=0 NormalZ=1 AngleXU=0 Radius=2
    g1: Circle CenterX=343.262 CenterY=300 CenterZ=0 NormalX=0 NormalY=0 NormalZ=1 AngleXU=0 Radius=2
    g2: Circle CenterX=343.262 CenterY=1063 CenterZ=0 NormalX=0 NormalY=0 NormalZ=1 AngleXU=0 Radius=2
    g3: Circle CenterX=343.262 CenterY=999.8 CenterZ=0 NormalX=0 NormalY=0 NormalZ=1 AngleXU=0 Radius=2
    g4: LineSegment [constr] StartX=343.262 StartY=1063 StartZ=0 EndX=343.262 EndY=999.8 EndZ=0
    g5: LineSegment [constr] StartX=343.262 StartY=999.8 StartZ=0 EndX=343.262 EndY=363.2 EndZ=0
    g6: LineSegment [constr] StartX=343.262 StartY=363.2 StartZ=0 EndX=343.262 EndY=300 EndZ=0
    g7: GeomPoint [constr] X=353.262 Y=301.263 Z=0
  constraints (21):
    c: Coincident(g4,g2)
    c: Vertical(g4)
    c: Coincident(g4,g5)
    c: Coincident(g5,g0)
    c: Vertical(g5)
    c: Coincident(g5,g6)
    c: Coincident(g6,g1)
    c: Vertical(g6)
    c: Coincident(g4,g3)
    c: Equal(g4,g6)
    c: DistanceY(g6,g6) = 63.2
    c: DistanceY(g2) = 1063
    c: DistanceY(g1) = 300
    c: Equal(g1,g0)
    c: Equal(g1,g3)
    c: Equal(g1,g2)
    c: Diameter(g1) = 4
    c: DistanceX(g1) = 343.262
    c: DistanceX(g7) = 353.262
    c: DistanceY(g7) = 301.263
    c: DistanceX(g1,g7) = 10
FEATURE [Sketcher::SketchObject] Sketch162
  ArcFitTolerance = 0
  AttachmentSupport = -> [BaseBend034]
  FullyConstrained = true
  MakeInternals = false
  MapMode = 5
  Placement = pos=(31.1979,356.594,0) rot=(0.998099,-0.043578,-0.043578;1.5727rad)
  sketch-geometry (11):
    g0: LineSegment [constr] StartX=20 StartY=15 StartZ=0 EndX=20 EndY=250 EndZ=0
    g1: LineSegment [constr] StartX=20 StartY=250 StartZ=0 EndX=20 EndY=485 EndZ=0
    g2: LineSegment [constr] StartX=20 StartY=485 StartZ=0 EndX=20 EndY=720 EndZ=0
    g3: LineSegment [constr] StartX=20 StartY=720 StartZ=0 EndX=20 EndY=955 EndZ=0
    g4: LineSegment [constr] StartX=20 StartY=955 StartZ=0 EndX=20 EndY=1190 EndZ=0
    g5: Circle CenterX=20 CenterY=15 CenterZ=0 NormalX=0 NormalY=0 NormalZ=1 AngleXU=0 Radius=1.7
    g6: Circle CenterX=20 CenterY=250 CenterZ=0 NormalX=0 NormalY=0 NormalZ=1 AngleXU=0 Radius=1.7
    g7: Circle CenterX=20 CenterY=485 CenterZ=0 NormalX=0 NormalY=0 NormalZ=1 AngleXU=0 Radius=1.7
    g8: Circle CenterX=20 CenterY=720 CenterZ=0 NormalX=0 NormalY=0 NormalZ=1 AngleXU=0 Radius=1.7
    g9: Circle CenterX=20 CenterY=955 CenterZ=0 NormalX=0 NormalY=0 NormalZ=1 AngleXU=0 Radius=1.7
    g10: Circle CenterX=20 CenterY=1190 CenterZ=0 NormalX=0 NormalY=0 NormalZ=1 AngleXU=0 Radius=1.7
  constraints (24):
    c: Vertical(g0)
    c: Coincident(g0,g1)
    c: Vertical(g1)
    c: Coincident(g1,g2)
    c: Vertical(g2)
    c: Coincident(g2,g3)
    c: Vertical(g3)
    c: Coincident(g3,g4)
    c: Vertical(g4)
    c: Equal(g0,g1)
    c: Equal(g1,g2)
    c: Equal(g2,g3)
    c: Equal(g3,g4)
    c: Coincident(g5,g0)
    c: Coincident(g6,g0)
    c: Coincident(g7,g1)
    c: Coincident(g8,g2)
    c: Coincident(g9,g3)
    c: Coincident(g10,g4)
    c: Equal(g5, g6-g10) x5
    c: Diameter(g5) = 3.4
    c: DistanceY(g10) = 1190
    c: DistanceY(g5) = 15
    c: DistanceX(g5) = 20
FEATURE [PartDesign::Pocket] Pocket095
  BaseFeature = -> Pocket075
  Direction = (0.0871557,0.996195,3e-16)
  Length = 5
  Length2 = 5
  Profile = -> Sketch162
  ReferenceAxis = -> Sketch162 [N_Axis]
  Suppressed = false
  Type = 0
FEATURE [PartDesign::Pocket] Pocket094
  BaseFeature = -> Pocket095
  Direction = (-1,0,0)
  Length = 5
  Length2 = 5
  Profile = -> Sketch161
  ReferenceAxis = -> Sketch161 [N_Axis]
  Suppressed = false
  Type = 0
FEATURE [PartDesign::Pocket] Pocket090
  BaseFeature = -> Pocket094
  Direction = (-1,0,0)
  Length = 5
  Length2 = 5
  Profile = -> Sketch159
  ReferenceAxis = -> Sketch159 [N_Axis]
  Suppressed = false
  Type = 0
FEATURE [PartDesign::Pocket] Pocket091
  BaseFeature = -> Pocket090
  Direction = (0.0871557,0.996195,3e-16)
  Length = 5
  Length2 = 5
  Profile = -> Sketch160
  ReferenceAxis = -> Sketch160 [N_Axis]
  Suppressed = false
  Type = 0
FEATURE [PartDesign::Body] Body095  label="door_base_pillar_material_0.45ansi"
  AllowCompound = false
  Group = -> [Binder083,BaseBend034,Pocket075,Binder092,Sketch159,Sketch160,Sketch161,Sketch162,Pocket095,Pocket094,Pocket090,Pocket091]
  Origin = -> Origin061
  Tip = -> Pocket091
COMPONENT P5 — recipe-attached ("led_holder2", modeled in this document).
Construction recipe (the document's own serialized feature program — sketch geometry with constraints, then the solid features built on it; lengths are millimeters unless a unit is written):

FEATURE [Sketcher::SketchObject] Sketch205
  ArcFitTolerance = 0
  AttachmentSupport = -> [XZ_Plane096]
  FullyConstrained = true
  MakeInternals = false
  MapMode = 5
  Placement = pos=(0,0,0) rot=(1,0,0;1.5708rad)
  sketch-geometry (4):
    g0: LineSegment StartX=0.1 StartY=485 StartZ=0 EndX=-14 EndY=485 EndZ=0
    g1: LineSegment StartX=-14 StartY=485 StartZ=0 EndX=-14 EndY=1590 EndZ=0
    g2: LineSegment StartX=-14 StartY=1590 StartZ=0 EndX=0.1 EndY=1590 EndZ=0
    g3: LineSegment StartX=0.1 StartY=1590 StartZ=0 EndX=0.1 EndY=485 EndZ=0
  constraints (13):
    c: Coincident(g0,g1)
    c: Coincident(g1,g2)
    c: Coincident(g2,g3)
    c: Coincident(g3,g0)
    c: Horizontal(g0)
    c: Horizontal(g2)
    c: Vertical(g1)
    c: Vertical(g3)
    c: DistanceY(g2) = 1590
    c: DistanceX(g2) = 0.1
    c: DistanceX(g1) = -14
    c: DistanceY(g0) = 485
    c: DistanceY(g3,g3) = 1105
FEATURE [PartDesign::Pad] Pad029
  Direction = (0,-1,2e-16)
  Length = 3
  Length2 = 10
  Placement = pos=(0,0,0) rot=(1,0,0;1.5708rad)
  Profile = -> Sketch205
  ReferenceAxis = -> Sketch205 [N_Axis]
  Suppressed = false
  Type = 0
FEATURE [PartDesign::Boolean] Boolean020
  BaseFeature = -> Pad029
  Group = -> [Compound060]
  Suppressed = false
  Type = 1
  UsePlacement = false
FEATURE [Sketcher::SketchObject] Sketch206
  ArcFitTolerance = 0
  AttachmentSupport = -> [XZ_Plane096]
  ExternalGeometry = -> [Sketch205]
  FullyConstrained = true
  MakeInternals = false
  MapMode = 5
  Placement = pos=(0,0,0) rot=(1,0,0;1.5708rad)
  sketch-geometry (13):
    g0: LineSegment [constr] StartX=-14 StartY=1590 StartZ=0 EndX=-6.95 EndY=1570 EndZ=0
    g1: LineSegment [constr] StartX=-6.95 StartY=1570 StartZ=0 EndX=0.1 EndY=1590 EndZ=0
    g2: LineSegment [constr] StartX=-14 StartY=485 StartZ=0 EndX=-6.95 EndY=505 EndZ=0
    g3: LineSegment [constr] StartX=-6.95 StartY=505 StartZ=0 EndX=0.1 EndY=485 EndZ=0
    g4: Circle CenterX=-6.95 CenterY=1570 CenterZ=0 NormalX=0 NormalY=0 NormalZ=1 AngleXU=0 Radius=1.7
    g5: Circle CenterX=-6.95 CenterY=1057.5 CenterZ=0 NormalX=0 NormalY=0 NormalZ=1 AngleXU=0 Radius=1.7
    g6: Circle CenterX=-6.95 CenterY=505 CenterZ=0 NormalX=0 NormalY=0 NormalZ=1 AngleXU=0 Radius=1.7
    g7: Circle CenterX=-6.95 CenterY=786.25 CenterZ=0 NormalX=0 NormalY=0 NormalZ=1 AngleXU=0 Radius=1.7
    g8: Circle CenterX=-6.95 CenterY=1288.75 CenterZ=0 NormalX=0 NormalY=0 NormalZ=1 AngleXU=0 Radius=1.7
    g9: LineSegment [constr] StartX=-6.95 StartY=505 StartZ=0 EndX=-6.95 EndY=771.25 EndZ=0
    g10: LineSegment [constr] StartX=-6.95 StartY=771.25 StartZ=0 EndX=-6.95 EndY=1037.5 EndZ=0
    g11: LineSegment [constr] StartX=-6.95 StartY=1037.5 StartZ=0 EndX=-6.95 EndY=1303.75 EndZ=0
    g12: LineSegment [constr] StartX=-6.95 StartY=1303.75 StartZ=0 EndX=-6.95 EndY=1570 EndZ=0
  constraints (34):
    c: Coincident(g-4,g0)
    c: Coincident(g0,g1)
    c: Coincident(g1,g-4)
    c: Coincident(g-3,g2)
    c: Coincident(g2,g3)
    c: Coincident(g3,g-3)
    c: Equal(g2,g3)
    c: Equal(g3,g0)
    c: Equal(g0,g1)
    c: DistanceY(g2,g2) = 20
    c: Coincident(g9,g2)
    c: Coincident(g11,g10)
    c: Coincident(g12,g0)
    c: Coincident(g4,g0)
    c: Coincident(g6,g2)
    c: Equal(g6,g5)
    c: Equal(g6,g4)
    c: Diameter(g6) = 3.4
    c: DistanceY(g10,g5) = 20
    c: Equal(g8,g7)
    c: Equal(g7,g6)
    c: Coincident(g9,g10)
    c: Vertical(g9)
    c: Vertical(g10)
    c: PointOnObject(g7,g9)
    c: Equal(g9,g10)
    c: Coincident(g11,g12)
    c: PointOnObject(g5,g11)
    c: PointOnObject(g8,g11)
    c: Equal(g11,g12)
    c: Equal(g10,g11)
    c: DistanceY(g8,g11) = 15
    c: DistanceY(g9,g7) = 15
    c: Vertical(g11)
FEATURE [PartDesign::Pocket] Pocket123
  BaseFeature = -> Boolean020
  Direction = (0,1,-2e-16)
  Length = 5
  Length2 = 5
  Midplane = true
  Profile = -> Sketch206
  ReferenceAxis = -> Sketch206 [N_Axis]
  Suppressed = false
  Type = 1
FEATURE [PartDesign::Body] Body120  label="led_holder2"
  AllowCompound = false
  Group = -> [Sketch205,Pad029,Boolean020,Sketch206,Pocket123]
  Origin = -> Origin096
  Placement = pos=(0,3.2,0) rot=(0,0,1;3.14159rad)
  Tip = -> Pocket123
COMPONENT P6 — recipe-attached ("sector_plexiglass_material_0.30ansi", modeled in this document).
Construction recipe (the document's own serialized feature program — sketch geometry with constraints, then the solid features built on it; lengths are millimeters unless a unit is written):

FEATURE [PartDesign::SubShapeBinder] Binder128
  BindCopyOnChange = 0
  BindMode = 0
  ClaimChildren = true
  Context = -> Body121 [Binder128.]
  Fuse = false
  MakeFace = true
  OffsetFill = false
  OffsetIntersection = false
  OffsetJoinType = 0
  OffsetOpenResult = false
  PartialLoad = false
  Relative = false
  Support = -> [Compound061]
  _Version = 2
FEATURE [PartDesign::FeaturePython] BaseBend049  label="sector_plexiglass_BaseBend"  # WARN: FeaturePython — macro-defined, semantics opaque (R4)
  BendSide = 1
  BendSketch = -> Binder128
  MidPlane = false
  Reverse = false
  Suppressed = false
  length = 425
  radius = 1
  thickness = 1
FEATURE [PartDesign::CoordinateSystem] Local_CS004
  AttacherType = Attacher::AttachEngine3D
  AttachmentOffset = pos=(0,0,0) rot=(0,-1,0;1.5708rad)
  AttachmentSupport = -> [Binder128]
  MapMode = 7
  Placement = pos=(284.188,-181.72,0) rot=(0.131421,-0.700974,-0.700974;2.88025rad)
FEATURE [Sketcher::SketchObject] Sketch208
  ArcFitTolerance = 0
  AttachmentSupport = -> [Local_CS004]
  FullyConstrained = true
  MakeInternals = false
  MapMode = 5
  Placement = pos=(284.188,-181.72,0) rot=(-0.131421,0.700974,0.700974;3.40294rad)
  expr: Constraints[4] = <<plexiglass_bottom_fix_array>>.Step * 1 mm - <<plexiglass_bottom_fix_sketch>>.Constraints.length + 2 mm
  expr: Constraints[6] = <<plexiglass_bottom_fix_array>>.SpanStart - <<plexiglass_bottom_fix_array>>.Step * 1 mm / 2
  sketch-geometry (7):
    g0: LineSegment StartX=-12 StartY=-63.3333 StartZ=0 EndX=-12 EndY=15 EndZ=0
    g1: LineSegment StartX=-1 StartY=10 StartZ=0 EndX=-1 EndY=-58.3333 EndZ=0
    g2: GeomPoint [constr] X=-1 Y=-24.1667 Z=0
    g3: LineSegment StartX=-7 StartY=10 StartZ=0 EndX=-1 EndY=10 EndZ=0
    g4: LineSegment StartX=-1 StartY=-58.3333 StartZ=0 EndX=-7 EndY=-58.3333 EndZ=0
    g5: ArcOfCircle CenterX=-7 CenterY=15 CenterZ=0 NormalX=0 NormalY=0 NormalZ=1 AngleXU=0 Radius=5 StartAngle=3.14159 EndAngle=4.71239
    g6: ArcOfCircle CenterX=-7 CenterY=-63.3333 CenterZ=0 NormalX=0 NormalY=0 NormalZ=1 AngleXU=0 Radius=5 StartAngle=1.5708 EndAngle=3.14159
  constraints (17):
    c: Coincident(g3,g1)
    c: Coincident(g1,g4)
    c: Vertical(g0)
    c: Vertical(g1)
    c: DistanceY(g1,g1) = 68.3333
    c: Symmetric(g4,g3,g2)
    c: DistanceY(g2) = -24.1667
    c: Horizontal(g3)
    c: Horizontal(g4)
    c: Tangent(g5,g3) = -1.5708
    c: Tangent(g5,g0) = 1.5708
    c: Tangent(g6,g4) = -1.5708
    c: Tangent(g6,g0) = 1.5708
    c: Equal(g6,g5)
    c: Radius(g6) = 5
    c: Distance(g-1,g0) = 12
    c: Distance(g-1,g1) = 1
FEATURE [PartDesign::Pocket] Pocket124
  BaseFeature = -> BaseBend049
  Direction = (0.362233,-0.932087,0)
  Length = 5
  Length2 = 5
  Midplane = true
  Profile = -> Sketch208
  ReferenceAxis = -> Sketch208 [N_Axis]
  Suppressed = false
  Type = 1
FEATURE [PartDesign::LinearPattern] LinearPattern
  Direction = -> Z_Axis097
  Length = 591.667
  Mode = 1
  Occurrences = 6
  Offset = 118.333
  Suppressed = false
  TransformMode = 0
  expr: Length = <<plexiglass_bottom_fix_array>>.Step
  expr: Offset = <<plexiglass_bottom_fix_array>>.Step
FEATURE [PartDesign::Mirrored] Mirrored015
  MirrorPlane = -> YZ_Plane097
  Suppressed = false
  TransformMode = 0
FEATURE [PartDesign::MultiTransform] MultiTransform001
  BaseFeature = -> Pocket124
  Originals = -> [Pocket124]
  Suppressed = false
  TransformMode = 0
  Transformations = -> [LinearPattern,Mirrored015]
FEATURE [Sketcher::SketchObject] Sketch242
  ArcFitTolerance = 0
  AttachmentOffset = pos=(0,35,0) rot=(0,0,1;0rad)
  AttachmentSupport = -> [Local_CS004]
  FullyConstrained = true
  MakeInternals = false
  MapMode = 5
  Placement = pos=(284.188,-181.72,35) rot=(-0.131421,0.700974,0.700974;3.40294rad)
  sketch-geometry (3):
    g0: Circle CenterX=-6.5 CenterY=0 CenterZ=0 NormalX=0 NormalY=0 NormalZ=1 AngleXU=0 Radius=1.7
    g1: GeomPoint [constr] X=-12 Y=0 Z=0
    g2: GeomPoint [constr] X=-1 Y=0 Z=0
  constraints (6):
    c: Diameter(g0) = 3.4
    c: PointOnObject(g1,g-1)
    c: PointOnObject(g2,g-1)
    c: DistanceX(g2) = -1
    c: DistanceX(g1) = -12
    c: Symmetric(g2,g1,g0)
FEATURE [PartDesign::Pocket] Pocket134
  BaseFeature = -> MultiTransform001
  Direction = (0.362233,-0.932087,0)
  Length = 5
  Length2 = 5
  Midplane = true
  Profile = -> Sketch242
  ReferenceAxis = -> Sketch242 [N_Axis]
  Suppressed = false
  Type = 1
FEATURE [PartDesign::LinearPattern] LinearPattern001
  Direction = -> Z_Axis097
  Length = 355
  Mode = 0
  Occurrences = 2
  Offset = 355
  Suppressed = false
  TransformMode = 0
FEATURE [PartDesign::Mirrored] Mirrored019
  MirrorPlane = -> YZ_Plane097
  Suppressed = false
  TransformMode = 0
FEATURE [PartDesign::MultiTransform] MultiTransform
  BaseFeature = -> Pocket134
  Originals = -> [Pocket134]
  Suppressed = false
  TransformMode = 0
  Transformations = -> [LinearPattern001,Mirrored019]
FEATURE [PartDesign::Body] Body121  label="sector_plexiglass_material_0.30ansi"
  AllowCompound = false
  Group = -> [Binder128,BaseBend049,Sketch208,Local_CS004,Pocket124,MultiTransform001,LinearPattern,Mirrored015,Sketch242,Pocket134,MultiTransform,LinearPattern001,Mirrored019]
  Origin = -> Origin097
  Tip = -> MultiTransform
COMPONENT P7 — recipe-attached ("basin_limiter", modeled in this document).
Construction recipe (the document's own serialized feature program — sketch geometry with constraints, then the solid features built on it; lengths are millimeters unless a unit is written):

FEATURE [PartDesign::SubShapeBinder] Binder131
  BindCopyOnChange = 0
  BindMode = 0
  ClaimChildren = true
  Fuse = false
  MakeFace = true
  OffsetFill = false
  OffsetIntersection = false
  OffsetJoinType = 0
  OffsetOpenResult = false
  PartialLoad = false
  Placement = pos=(0,0,0) rot=(0,0,1;3.14159rad)
  Relative = false
  Support = -> [Compound064]
  _Version = 2
FEATURE [PartDesign::Pad] Pad030
  Direction = (0,0,1)
  Length = 3
  Length2 = 10
  Placement = pos=(0,0,0) rot=(0,0,1;3.14159rad)
  Profile = -> Binder131
  Refine = true
  Suppressed = false
  Type = 0
FEATURE [PartDesign::Boolean] Boolean022
  BaseFeature = -> Pad030
  Group = -> [Compound065]
  Refine = true
  Suppressed = false
  Type = 1
  UsePlacement = false
FEATURE [PartDesign::SubShapeBinder] Binder133
  BindCopyOnChange = 0
  BindMode = 0
  ClaimChildren = true
  Context = -> Body122 [Binder133.]
  Fuse = false
  MakeFace = true
  OffsetFill = false
  OffsetIntersection = false
  OffsetJoinType = 0
  OffsetOpenResult = false
  PartialLoad = false
  Relative = true
  Support = -> [Sketch210]
  _Version = 2
FEATURE [PartDesign::Body] Body122  label="basin_limiter"
  AllowCompound = false
  Group = -> [Binder131,Pad030,Boolean022,Binder133]
  Origin = -> Origin098
  Placement = pos=(0,0,21) rot=(0,0,1;0rad)
  Tip = -> Boolean022
COMPONENT P8 — recipe-attached ("Body", modeled in this document).
Construction recipe (the document's own serialized feature program — sketch geometry with constraints, then the solid features built on it; lengths are millimeters unless a unit is written):

FEATURE [Sketcher::SketchObject] Sketch223
  ArcFitTolerance = 0
  AttachmentOffset = pos=(0,0,0) rot=(0,1,0;0.523599rad)
  AttachmentSupport = -> [XZ_Plane102]
  FullyConstrained = true
  MakeInternals = false
  MapMode = 5
  Placement = pos=(0,0,0) rot=(0.935113,0.250563,0.250563;1.63783rad)
  expr: Constraints[15] = <<sleeve_outer_sketch>>.Constraints.flange_max_r + 1 mm
  expr: Constraints[16] = <<sleeve_outer_sketch>>.Constraints.max_r + 1 mm
  sketch-geometry (8):
    g0: ArcOfCircle CenterX=39.25 CenterY=3 CenterZ=0 NormalX=0 NormalY=0 NormalZ=1 AngleXU=0 Radius=3 StartAngle=3.14159 EndAngle=4.71239
    g1: LineSegment StartX=36.25 StartY=3 StartZ=0 EndX=36.25 EndY=48.4 EndZ=0
    g2: LineSegment StartX=36.25 StartY=48.4 StartZ=0 EndX=21.25 EndY=48.4 EndZ=0
    g3: LineSegment StartX=21.25 StartY=48.4 StartZ=0 EndX=21.25 EndY=40.4 EndZ=0
    g4: LineSegment StartX=0 StartY=0 StartZ=0 EndX=39.25 EndY=0 EndZ=0
    g5: LineSegment StartX=21.25 StartY=40.4 StartZ=0 EndX=0 EndY=40.4 EndZ=0
    g6: LineSegment StartX=0 StartY=40.4 StartZ=0 EndX=0 EndY=0 EndZ=0
    g7: GeomPoint [constr] X=21.25 Y=48.4 Z=0
  constraints (21):
    c: PointOnObject(g0,g-1)
    c: Vertical(g1)
    c: Coincident(g2,g1)
    c: Horizontal(g2)
    c: Vertical(g3)
    c: Tangent(g1,g0) = 1.5708
    c: Coincident(g4,g-1)
    c: Tangent(g4,g0) = -1.5708
    c: Radius(g0) = 3
    c: Coincident(g5,g3)
    c: PointOnObject(g5,g-2)
    c: Horizontal(g5)
    c: Coincident(g6,g5)
    c: Coincident(g6,g4)
    c: DistanceY(g6,g6) = 40.4
    c: DistanceX(g1) = 36.25
    c: DistanceX(g7) = 21.25
    c: DistanceY(g7,g3) = -8
    c: PointOnObject(g7,g2)
    c: PointOnObject(g7,g3)
    c: Coincident(g2,g3)
FEATURE [Sketcher::SketchObject] Sketch224
  ArcFitTolerance = 0
  AttachmentSupport = -> [XY_Plane102]
  FullyConstrained = true
  MakeInternals = false
  MapMode = 5
  expr: Constraints[10] = <<sleeve_outer_sketch>>.Constraints.max_r + 1 mm
  sketch-geometry (7):
    g0: LineSegment StartX=1.3e-15 StartY=21.4809 StartZ=0 EndX=0 EndY=0.46188 EndZ=0
    g1: LineSegment StartX=0 StartY=0.46188 StartZ=0 EndX=18.203 EndY=10.9714 EndZ=0
    g2: LineSegment [constr] StartX=0 StartY=0 StartZ=0 EndX=-0.2 EndY=0.34641 EndZ=0
    g3: LineSegment [constr] StartX=-0.2 StartY=0.34641 StartZ=0 EndX=0 EndY=0.46188 EndZ=0
    g4: ArcOfCircle CenterX=0 CenterY=0.46188 CenterZ=0 NormalX=0 NormalY=0 NormalZ=1 AngleXU=0 Radius=21.0191 StartAngle=0.648827 EndAngle=1.5708
    g5: ArcOfCircle CenterX=19.1382 CenterY=14.9754 CenterZ=0 NormalX=0 NormalY=0 NormalZ=1 AngleXU=0 Radius=3 StartAngle=3.79042 EndAngle=5.23599
    g6: LineSegment StartX=18.203 StartY=10.9714 StartZ=0 EndX=20.6382 EndY=12.3774 EndZ=0
  constraints (19):
    c: PointOnObject(g0,g-2)
    c: PointOnObject(g0,g-2)
    c: Coincident(g0,g1)
    c: Angle(g1) = 0.523599
    c: Distance(g-1,g1) = 0.4
    c: Coincident(g4,g0)
    c: Coincident(g2,g3)
    c: Coincident(g3,g0)
    c: Perpendicular(g3,g2)
    c: Parallel(g3,g1)
    c: Distance(g2,g1) = 21.25
    c: Coincident(g6,g1)
    c: Parallel(g6,g1)
    c: Tangent(g5,g4) = 1.5708
    c: PointOnObject(g1,g4)
    c: Coincident(g-1,g2)
    c: Coincident(g4,g0)
    c: Tangent(g6,g5) = -1.5708
    c: Radius(g5) = 3
FEATURE [PartDesign::Pad] Pad034
  Direction = (0.5,-0.866025,1e-16)
  Length = 0.4
  Length2 = 10
  Placement = pos=(0,0,0) rot=(1,0,0;1.5708rad)
  Profile = -> Sketch223
  ReferenceAxis = -> Sketch223 [N_Axis]
  Reversed = true
  Suppressed = false
  Type = 0
FEATURE [PartDesign::Pad] Pad035
  BaseFeature = -> Pad034
  Direction = (0,0,1)
  Length = 50
  Length2 = 10
  Placement = pos=(0,0,0) rot=(1,0,0;1.5708rad)
  Profile = -> Sketch224
  ReferenceAxis = -> Sketch224 [N_Axis]
  Suppressed = false
  Type = 0
FEATURE [PartDesign::Mirrored] Mirrored018
  BaseFeature = -> Pad035
  MirrorPlane = -> YZ_Plane102
  Originals = -> [Pad034,Pad035]
  Placement = pos=(0,0,0) rot=(1,0,0;1.5708rad)
  Suppressed = false
  TransformMode = 0
FEATURE [PartDesign::Body] Body125  label="Body"
  AllowCompound = false
  Group = -> [Sketch223,Sketch224,Pad034,Pad035,Mirrored018]
  Origin = -> Origin102
  Tip = -> Mirrored018
COMPONENT P9 — recipe-attached ("UV_driver_holder_material_0.30ansi", modeled in this document).
Construction recipe (the document's own serialized feature program — sketch geometry with constraints, then the solid features built on it; lengths are millimeters unless a unit is written):

FEATURE [PartDesign::SubShapeBinder] Binder149
  BindCopyOnChange = 0
  BindMode = 0
  ClaimChildren = true
  Context = -> <external composit_full_size3_composit_cut.FCStd>#Link026 [Binder149.]
  Fuse = false
  MakeFace = true
  OffsetFill = false
  OffsetIntersection = false
  OffsetJoinType = 0
  OffsetOpenResult = false
  PartialLoad = false
  Placement = pos=(0,0,0) rot=(1,0,0;1.5708rad)
  Relative = false
  Support = -> [Sketch225]
  _Version = 2
  expr: Support = <<UV_driver_holder_base_Sketch>>._self
FEATURE [PartDesign::FeaturePython] BaseBend050  label="UV_driver_holder_BaseBend"  # WARN: FeaturePython — macro-defined, semantics opaque (R4)
  BendSide = 0
  BendSketch = -> Binder149
  MidPlane = true
  Reverse = false
  Suppressed = false
  length = 20
  radius = 0.1
  thickness = 0.3
FEATURE [Sketcher::SketchObject] Sketch269
  ArcFitTolerance = 0
  AttachmentOffset = pos=(31.5,10,0) rot=(0,0,1;0rad)
  AttachmentSupport = -> [XY_Plane103]
  FullyConstrained = true
  MakeInternals = false
  MapMode = 5
  Placement = pos=(31.5,10,0) rot=(0,0,1;0rad)
  expr: .AttachmentOffset.Base.x = <<UV_driver_holder_base_Sketch>>.Constraints.total_width / 2
  expr: .AttachmentOffset.Base.y = <<UV_driver_holder_BaseBend>>.length / 2
  sketch-geometry (3):
    g0: LineSegment StartX=-3 StartY=0 StartZ=0 EndX=0 EndY=0 EndZ=0
    g1: LineSegment StartX=0 StartY=0 StartZ=0 EndX=0 EndY=-3 EndZ=0
    g2: ArcOfCircle CenterX=-3 CenterY=-3 CenterZ=0 NormalX=0 NormalY=0 NormalZ=1 AngleXU=0 Radius=3 StartAngle=1e-16 EndAngle=1.5708
  constraints (7):
    c: PointOnObject(g0,g-1)
    c: Coincident(g0,g-1)
    c: Coincident(g0,g1)
    c: PointOnObject(g1,g-2)
    c: Tangent(g2,g0) = 1.5708
    c: Tangent(g2,g1) = 1.5708
    c: Radius(g2) = 3
FEATURE [PartDesign::Pocket] Pocket145
  BaseFeature = -> BaseBend050
  Direction = (0,0,-1)
  Length = 5
  Length2 = 5
  Profile = -> Sketch269
  ReferenceAxis = -> Sketch269 [N_Axis]
  Reversed = true
  Suppressed = false
  Type = 0
FEATURE [PartDesign::Mirrored] Mirrored023
  MirrorPlane = -> YZ_Plane103
  Suppressed = false
  TransformMode = 0
FEATURE [PartDesign::Mirrored] Mirrored024
  MirrorPlane = -> XZ_Plane103
  Suppressed = false
  TransformMode = 0
FEATURE [PartDesign::MultiTransform] MultiTransform002
  BaseFeature = -> Pocket145
  Originals = -> [Pocket145]
  Suppressed = false
  TransformMode = 0
  Transformations = -> [Mirrored023,Mirrored024]
FEATURE [PartDesign::Boolean] Boolean052
  BaseFeature = -> MultiTransform002
  Group = -> [Compound104]
  Suppressed = false
  Type = 1
  UsePlacement = true
FEATURE [PartDesign::Body] Body126  label="UV_driver_holder_material_0.30ansi"
  AllowCompound = false
  Group = -> [BaseBend050,Binder149,Sketch269,Pocket145,MultiTransform002,Mirrored023,Mirrored024,Boolean052]
  Origin = -> Origin103
  Tip = -> Boolean052
COMPONENT P10 — recipe-attached ("bottom_bearing", modeled in this document).
Construction recipe (the document's own serialized feature program — sketch geometry with constraints, then the solid features built on it; lengths are millimeters unless a unit is written):

FEATURE [Sketcher::SketchObject] Sketch227  label="bottom_bearing_Sketch"
  ArcFitTolerance = 0
  AttachmentSupport = -> [XZ_Plane104]
  FullyConstrained = true
  MakeInternals = false
  MapMode = 5
  Placement = pos=(0,0,0) rot=(1,0,0;1.5708rad)
  sketch-geometry (4):
    g0: LineSegment StartX=37.5 StartY=0 StartZ=0 EndX=50 EndY=0 EndZ=0
    g1: LineSegment StartX=50 StartY=0 StartZ=0 EndX=50 EndY=19 EndZ=0
    g2: LineSegment StartX=50 StartY=19 StartZ=0 EndX=37.5 EndY=19 EndZ=0
    g3: LineSegment StartX=37.5 StartY=19 StartZ=0 EndX=37.5 EndY=0 EndZ=0
  constraints (12):
    c: Coincident(g0,g1)
    c: Coincident(g1,g2)
    c: Coincident(g2,g3)
    c: Coincident(g3,g0)
    c: Horizontal(g0)
    c: Horizontal(g2)
    c: Vertical(g1)
    c: Vertical(g3)
    c: PointOnObject(g0,g-1)
    c: DistanceY(g3,g3) = 19  'height'
    c: DistanceX(g0) = 37.5  'inner_r'
    c: DistanceX(g0) = 50  'outer_r'
FEATURE [PartDesign::Revolution] Revolution002
  Angle = 360
  Angle2 = 60
  Axis = (0,2e-16,1)
  Base = (0,0,0)
  Placement = pos=(0,0,0) rot=(1,0,0;1.5708rad)
  Profile = -> Sketch227
  ReferenceAxis = -> Sketch227 [V_Axis]
  Reversed = true
  Suppressed = false
  Type = 0
FEATURE [PartDesign::Body] Body127  label="bottom_bearing"
  AllowCompound = false
  Group = -> [Sketch227,Revolution002]
  Origin = -> Origin104
  Tip = -> Revolution002
COMPONENT P11 — recipe-attached ("bottom_caprolon", modeled in this document).
Construction recipe (the document's own serialized feature program — sketch geometry with constraints, then the solid features built on it; lengths are millimeters unless a unit is written):

FEATURE [Sketcher::SketchObject] Sketch228
  ArcFitTolerance = 0
  AttachmentSupport = -> [XZ_Plane105]
  FullyConstrained = true
  MakeInternals = false
  MapMode = 5
  Placement = pos=(0,0,0) rot=(1,0,0;1.5708rad)
  expr: Constraints[12] = <<bottom_bearing_Sketch>>.Constraints.inner_r - 0.5 mm
  expr: Constraints[13] = <<bottom_bearing_Sketch>>.Constraints.outer_r
  expr: Constraints[16] = 61.3 mm - <<bottom_bearing_Sketch>>.Constraints.height
  sketch-geometry (6):
    g0: LineSegment StartX=37 StartY=0 StartZ=0 EndX=37 EndY=5 EndZ=0
    g1: LineSegment StartX=37 StartY=5 StartZ=0 EndX=50 EndY=5 EndZ=0
    g2: LineSegment StartX=50 StartY=5 StartZ=0 EndX=50 EndY=47.3 EndZ=0
    g3: LineSegment StartX=50 StartY=47.3 StartZ=0 EndX=0 EndY=47.3 EndZ=0
    g4: LineSegment StartX=0 StartY=47.3 StartZ=0 EndX=0 EndY=0 EndZ=0
    g5: LineSegment StartX=0 StartY=0 StartZ=0 EndX=37 EndY=0 EndZ=0
  constraints (17):
    c: Vertical(g0)
    c: Coincident(g0,g1)
    c: Coincident(g1,g2)
    c: Vertical(g2)
    c: Coincident(g2,g3)
    c: Horizontal(g3)
    c: Coincident(g3,g4)
    c: Vertical(g4)
    c: Coincident(g4,g5)
    c: Coincident(g5,g0)
    c: Horizontal(g5)
    c: DistanceY(g0,g0) = 5
    c: DistanceX(g0) = 37
    c: DistanceX(g1) = 50
    c: Horizontal(g1)
    c: Coincident(g4,g-1)
    c: DistanceY(g2,g2) = 42.3
FEATURE [PartDesign::Revolution] Revolution003
  Angle = 360
  Angle2 = 60
  Axis = (0,2e-16,1)
  Base = (0,0,0)
  Placement = pos=(0,0,0) rot=(1,0,0;1.5708rad)
  Profile = -> Sketch228
  ReferenceAxis = -> Sketch228 [V_Axis]
  Reversed = true
  Suppressed = false
  Type = 0
FEATURE [PartDesign::Boolean] Boolean036
  BaseFeature = -> Revolution003
  Group = -> [Compound085]
  Suppressed = false
  Type = 1
  UsePlacement = false
FEATURE [PartDesign::Body] Body128  label="bottom_caprolon"
  AllowCompound = false
  Group = -> [Sketch228,Revolution003,Boolean036]
  Origin = -> Origin105
  Placement = pos=(0,0,14) rot=(0,0,1;0rad)
  Tip = -> Boolean036
COMPONENT P12 — recipe-attached ("wheel", modeled in this document).
Construction recipe (the document's own serialized feature program — sketch geometry with constraints, then the solid features built on it; lengths are millimeters unless a unit is written):

FEATURE [Sketcher::SketchObject] Sketch229
  ArcFitTolerance = 0
  AttachmentSupport = -> [XY_Plane106]
  FullyConstrained = true
  MakeInternals = false
  MapMode = 5
  sketch-geometry (13):
    g0: LineSegment [constr] StartX=-15.05 StartY=-24.05 StartZ=0 EndX=-15.05 EndY=24.05 EndZ=0
    g1: LineSegment [constr] StartX=-15.05 StartY=24.05 StartZ=0 EndX=15.05 EndY=24.05 EndZ=0
    g2: LineSegment [constr] StartX=15.05 StartY=24.05 StartZ=0 EndX=15.05 EndY=-24.05 EndZ=0
    g3: LineSegment [constr] StartX=15.05 StartY=-24.05 StartZ=0 EndX=-15.05 EndY=-24.05 EndZ=0
    g4: GeomPoint [constr] X=2e-16 Y=0 Z=0
    g5: Circle CenterX=15.05 CenterY=24.05 CenterZ=0 NormalX=0 NormalY=0 NormalZ=1 AngleXU=0 Radius=3.15
    g6: Circle CenterX=-15.05 CenterY=24.05 CenterZ=0 NormalX=0 NormalY=0 NormalZ=1 AngleXU=0 Radius=3.15
    g7: Circle CenterX=-15.05 CenterY=-24.05 CenterZ=0 NormalX=0 NormalY=0 NormalZ=1 AngleXU=0 Radius=3.15
    g8: Circle CenterX=15.05 CenterY=-24.05 CenterZ=0 NormalX=0 NormalY=0 NormalZ=1 AngleXU=0 Radius=3.15
    g9: GeomPoint [constr] X=-18.2 Y=24.05 Z=0
    g10: GeomPoint [constr] X=18.2 Y=24.05 Z=0
    g11: GeomPoint [constr] X=15.05 Y=-27.2 Z=0
    g12: GeomPoint [constr] X=15.05 Y=27.2 Z=0
  constraints (28):
    c: Coincident(g0,g1)
    c: Coincident(g1,g2)
    c: Coincident(g2,g3)
    c: Coincident(g3,g0)
    c: Horizontal(g1)
    c: Horizontal(g3)
    c: Vertical(g0)
    c: Vertical(g2)
    c: Symmetric(g1,g0,g4)
    c: Coincident(g4,g-1)
    c: Coincident(g5,g1)
    c: Coincident(g6,g0)
    c: Coincident(g7,g0)
    c: Coincident(g8,g2)
    c: PointOnObject(g9,g6)
    c: PointOnObject(g10,g5)
    c: PointOnObject(g11,g8)
    c: PointOnObject(g12,g5)
    c: Vertical(g5,g12)
    c: Horizontal(g5,g10)
    c: Horizontal(g6,g9)
    c: Vertical(g8,g11)
    c: Equal(g5,g6)
    c: Equal(g6,g7)
    c: Equal(g7,g8)
    c: DistanceX(g9,g10) = 36.4
    c: DistanceY(g11,g12) = 54.4
    c: Diameter(g5) = 6.3
FEATURE [Sketcher::SketchObject] Sketch230
  ArcFitTolerance = 0
  AttachmentSupport = -> [XY_Plane106]
  FullyConstrained = true
  MakeInternals = false
  MapMode = 5
  sketch-geometry (5):
    g0: LineSegment StartX=-22.5 StartY=-30 StartZ=0 EndX=-22.5 EndY=30 EndZ=0
    g1: LineSegment StartX=-22.5 StartY=30 StartZ=0 EndX=22.5 EndY=30 EndZ=0
    g2: LineSegment StartX=22.5 StartY=30 StartZ=0 EndX=22.5 EndY=-30 EndZ=0
    g3: LineSegment StartX=22.5 StartY=-30 StartZ=0 EndX=-22.5 EndY=-30 EndZ=0
    g4: GeomPoint [constr] X=0 Y=0 Z=0
  constraints (12):
    c: Coincident(g0,g1)
    c: Coincident(g1,g2)
    c: Coincident(g2,g3)
    c: Coincident(g3,g0)
    c: Horizontal(g1)
    c: Horizontal(g3)
    c: Vertical(g0)
    c: Vertical(g2)
    c: Symmetric(g1,g0,g4)
    c: Coincident(g4,g-1)
    c: DistanceY(g2,g2) = 60
    c: DistanceX(g1,g1) = 45
FEATURE [PartDesign::Pad] Pad036
  Direction = (0,0,1)
  Length = 60.3
  Length2 = 10
  Profile = -> Sketch230
  ReferenceAxis = -> Sketch230 [N_Axis]
  Suppressed = false
  Type = 0
FEATURE [PartDesign::Body] Body129  label="wheel"
  AllowCompound = false
  Group = -> [Sketch229,Sketch230,Pad036]
  Origin = -> Origin106
  Tip = -> Pad036
COMPONENT P13 — recipe-attached ("Body130", modeled in this document).
Construction recipe (the document's own serialized feature program — sketch geometry with constraints, then the solid features built on it; lengths are millimeters unless a unit is written):

FEATURE [PartDesign::SubShapeBinder] Binder136
  BindCopyOnChange = 0
  BindMode = 0
  ClaimChildren = true
  Context = -> Body130 [Binder136.]
  Fuse = false
  MakeFace = true
  OffsetFill = false
  OffsetIntersection = false
  OffsetJoinType = 0
  OffsetOpenResult = false
  PartialLoad = false
  Relative = false
  Support = -> [Connect004]
  _Version = 2
FEATURE [PartDesign::Pad] Pad037
  Direction = (0,0,1)
  Length = 1
  Length2 = 10
  Profile = -> Binder136
  Suppressed = false
  Type = 0
FEATURE [PartDesign::Boolean] Boolean037
  BaseFeature = -> Pad037
  Group = -> [Compound086]
  Refine = true
  Suppressed = false
  Type = 0
  UsePlacement = false
FEATURE [PartDesign::Boolean] Boolean038
  BaseFeature = -> Boolean037
  Group = -> [Populate053]
  Suppressed = false
  Type = 1
  UsePlacement = false
FEATURE [PartDesign::Body] Body130
  AllowCompound = false
  Group = -> [Binder136,Pad037,Boolean037,Boolean038]
  Origin = -> Origin107
  Tip = -> Boolean038
COMPONENT P14 — recipe-attached ("small_bearing", modeled in this document).
Construction recipe (the document's own serialized feature program — sketch geometry with constraints, then the solid features built on it; lengths are millimeters unless a unit is written):

FEATURE [Sketcher::SketchObject] Sketch233  label="small_bearing_Sketch"
  ArcFitTolerance = 0
  AttachmentSupport = -> [XZ_Plane108]
  FullyConstrained = true
  MakeInternals = false
  MapMode = 5
  Placement = pos=(0,0,0) rot=(1,0,0;1.5708rad)
  sketch-geometry (4):
    g0: LineSegment StartX=6 StartY=0 StartZ=0 EndX=13 EndY=0 EndZ=0
    g1: LineSegment StartX=13 StartY=0 StartZ=0 EndX=13 EndY=8.9 EndZ=0
    g2: LineSegment StartX=13 StartY=8.9 StartZ=0 EndX=6 EndY=8.9 EndZ=0
    g3: LineSegment StartX=6 StartY=8.9 StartZ=0 EndX=6 EndY=0 EndZ=0
  constraints (12):
    c: Coincident(g0,g1)
    c: Coincident(g1,g2)
    c: Coincident(g2,g3)
    c: Coincident(g3,g0)
    c: Horizontal(g0)
    c: Horizontal(g2)
    c: Vertical(g1)
    c: Vertical(g3)
    c: PointOnObject(g0,g-1)
    c: DistanceY(g3,g3) = 8.9
    c: DistanceX(g0) = 6
    c: DistanceX(g0) = 13
FEATURE [PartDesign::Revolution] Revolution004
  Angle = 360
  Angle2 = 60
  Axis = (0,2e-16,1)
  Base = (0,0,0)
  Placement = pos=(0,0,0) rot=(1,0,0;1.5708rad)
  Profile = -> Sketch233
  ReferenceAxis = -> Sketch233 [V_Axis]
  Reversed = true
  Suppressed = false
  Type = 0
FEATURE [PartDesign::Body] Body131  label="small_bearing"
  AllowCompound = false
  Group = -> [Sketch233,Revolution004]
  Origin = -> Origin108
  Tip = -> Revolution004
COMPONENT P15 — recipe-attached ("sleeve_outer2", modeled in this document).
Construction recipe (the document's own serialized feature program — sketch geometry with constraints, then the solid features built on it; lengths are millimeters unless a unit is written):

FEATURE [Sketcher::SketchObject] Sketch234  label="sleeve_outer_sketch001"
  ArcFitTolerance = 0
  AttachmentSupport = -> [XZ_Plane110]
  FullyConstrained = true
  MakeInternals = false
  MapMode = 5
  Placement = pos=(0,0,0) rot=(1,0,0;1.5708rad)
  expr: Constraints[13] = <<sleeve_inner_sketch001>>.Constraints.outer_r + 0.25 mm
  sketch-geometry (6):
    g0: LineSegment StartX=13.25 StartY=74.7 StartZ=0 EndX=13.25 EndY=0 EndZ=0
    g1: LineSegment StartX=13.25 StartY=0 StartZ=0 EndX=35.25 EndY=0 EndZ=0
    g2: LineSegment StartX=35.25 StartY=0 StartZ=0 EndX=35.25 EndY=7 EndZ=0
    g3: LineSegment StartX=35.25 StartY=7 StartZ=0 EndX=20.25 EndY=7 EndZ=0
    g4: LineSegment StartX=20.25 StartY=7 StartZ=0 EndX=20.25 EndY=74.7 EndZ=0
    g5: LineSegment StartX=20.25 StartY=74.7 StartZ=0 EndX=13.25 EndY=74.7 EndZ=0
  constraints (20):
    c: PointOnObject(g0,g-1)
    c: Vertical(g0)
    c: Coincident(g0,g1)
    c: PointOnObject(g1,g-1)
    c: Coincident(g1,g2)
    c: Vertical(g2)
    c: Coincident(g2,g3)
    c: Horizontal(g3)
    c: Coincident(g3,g4)
    c: Vertical(g4)
    c: Coincident(g4,g5)
    c: Coincident(g5,g0)
    c: Horizontal(g5)
    c: DistanceX(g0) = 13.25
    c: DistanceX(g5,g5) = 7
    c: DistanceX(g3,g3) = 15
    c: DistanceY(g2,g2) = 7  'flange_height'
    c: DistanceY(g0,g0) = 74.7
    c: DistanceX(g3) = 20.25  'max_r'
    c: DistanceX(g1) = 35.25  'flange_max_r'
FEATURE [PartDesign::Revolution] Revolution006
  Angle = 360
  Angle2 = 60
  Axis = (0,2e-16,1)
  Base = (0,0,0)
  Placement = pos=(0,0,0) rot=(1,0,0;1.5708rad)
  Profile = -> Sketch234
  ReferenceAxis = -> Sketch234 [V_Axis]
  Reversed = true
  Suppressed = false
  Type = 0
FEATURE [PartDesign::Boolean] Boolean039
  BaseFeature = -> Revolution006
  Group = -> [Compound087]
  Suppressed = false
  Type = 1
  UsePlacement = false
FEATURE [PartDesign::CoordinateSystem] Local_CS035  label="sleeve2_outer_flange_LCS"
  AttacherType = Attacher::AttachEngine3D
  AttachmentSupport = -> [XY_Plane110]
  MapMode = 5
FEATURE [PartDesign::CoordinateSystem] Local_CS036  label="sleeve2_outer_end_LCS"
  AttacherType = Attacher::AttachEngine3D
  AttachmentOffset = pos=(0,0,74.7) rot=(0,0,1;0rad)
  AttachmentSupport = -> [XY_Plane110]
  MapMode = 5
  Placement = pos=(0,0,74.7) rot=(0,0,1;0rad)
FEATURE [PartDesign::Body] Body132  label="sleeve_outer2"
  AllowCompound = false
  Group = -> [Sketch234,Revolution006,Boolean039,Local_CS035,Local_CS036]
  Origin = -> Origin110
  Tip = -> Boolean039
COMPONENT P16 — recipe-attached ("sleeve_inner2", modeled in this document).
Construction recipe (the document's own serialized feature program — sketch geometry with constraints, then the solid features built on it; lengths are millimeters unless a unit is written):

FEATURE [Sketcher::SketchObject] Sketch235  label="sleeve_inner_sketch001"
  ArcFitTolerance = 0
  AttachmentSupport = -> [XZ_Plane101]
  FullyConstrained = true
  MakeInternals = false
  MapMode = 5
  Placement = pos=(0,0,0) rot=(1,0,0;1.5708rad)
  sketch-geometry (6):
    g0: LineSegment StartX=5 StartY=83.7 StartZ=0 EndX=5 EndY=0 EndZ=0
    g1: LineSegment StartX=5 StartY=0 StartZ=0 EndX=33 EndY=0 EndZ=0
    g2: LineSegment StartX=33 StartY=0 StartZ=0 EndX=33 EndY=5 EndZ=0
    g3: LineSegment StartX=33 StartY=5 StartZ=0 EndX=13 EndY=5 EndZ=0
    g4: LineSegment StartX=13 StartY=5 StartZ=0 EndX=13 EndY=83.7 EndZ=0
    g5: LineSegment StartX=13 StartY=83.7 StartZ=0 EndX=5 EndY=83.7 EndZ=0
  constraints (19):
    c: PointOnObject(g0,g-1)
    c: Vertical(g0)
    c: Coincident(g0,g1)
    c: PointOnObject(g1,g-1)
    c: Coincident(g1,g2)
    c: Vertical(g2)
    c: Coincident(g2,g3)
    c: Horizontal(g3)
    c: Coincident(g3,g4)
    c: Vertical(g4)
    c: Coincident(g4,g5)
    c: Coincident(g5,g0)
    c: Horizontal(g5)
    c: DistanceX(g0) = 5  'inner_r'
    c: DistanceX(g0,g3) = 8
    c: DistanceY(g2,g2) = 5
    c: DistanceX(g3,g3) = 20
    c: DistanceX(g3) = 13  'outer_r'
    c: DistanceY(g0) = 83.7
FEATURE [PartDesign::Revolution] Revolution005
  Angle = 360
  Angle2 = 60
  Axis = (0,2e-16,1)
  Base = (0,0,0)
  Placement = pos=(0,0,0) rot=(1,0,0;1.5708rad)
  Profile = -> Sketch235
  ReferenceAxis = -> Sketch235 [V_Axis]
  Reversed = true
  Suppressed = false
  Type = 0
FEATURE [PartDesign::Boolean] Boolean040
  BaseFeature = -> Revolution005
  Group = -> [Compound088]
  Suppressed = false
  Type = 1
  UsePlacement = false
FEATURE [PartDesign::CoordinateSystem] Local_CS033  label="sleeve_inner2_flange_top_LCS"
  AttacherType = Attacher::AttachEngine3D
  AttachmentOffset = pos=(0,0,5) rot=(0,0,1;0rad)
  AttachmentSupport = -> [XY_Plane101]
  MapMode = 5
  Placement = pos=(0,0,5) rot=(0,0,1;0rad)
FEATURE [PartDesign::CoordinateSystem] Local_CS034  label="sleeve_inner2_end_LCS"
  AttacherType = Attacher::AttachEngine3D
  AttachmentOffset = pos=(0,0,83.7) rot=(0,0,1;0rad)
  AttachmentSupport = -> [XY_Plane101]
  MapMode = 5
  Placement = pos=(0,0,83.7) rot=(0,0,1;0rad)
FEATURE [PartDesign::Body] Body133  label="sleeve_inner2"
  AllowCompound = false
  Group = -> [Sketch235,Revolution005,Boolean040,Local_CS033,Local_CS034]
  Origin = -> Origin111
  Tip = -> Boolean040
COMPONENT P17 — recipe-attached ("wire_holder_material_0.30ansi", modeled in this document).
Construction recipe (the document's own serialized feature program — sketch geometry with constraints, then the solid features built on it; lengths are millimeters unless a unit is written):

FEATURE [PartDesign::SubShapeBinder] Binder137
  BindCopyOnChange = 0
  BindMode = 0
  ClaimChildren = true
  Context = -> Body134 [Binder137.]
  Fuse = false
  MakeFace = true
  OffsetFill = false
  OffsetIntersection = false
  OffsetJoinType = 0
  OffsetOpenResult = false
  PartialLoad = false
  Relative = false
  Support = -> [Sketch236]
  _Version = 2
FEATURE [PartDesign::FeaturePython] BaseBend051  # WARN: FeaturePython — macro-defined, semantics opaque (R4)
  BendSide = 0
  BendSketch = -> Binder137
  MidPlane = false
  Reverse = false
  Suppressed = false
  length = 830
  radius = 0.1
  thickness = 0.3
FEATURE [PartDesign::Boolean] Boolean041
  BaseFeature = -> BaseBend051
  Group = -> [Compound089]
  Suppressed = false
  Type = 1
  UsePlacement = false
FEATURE [PartDesign::Body] Body134  label="wire_holder_material_0.30ansi"
  AllowCompound = false
  Group = -> [Binder137,BaseBend051,Boolean041]
  Origin = -> Origin112
  Tip = -> Boolean041
COMPONENT P18 — recipe-attached ("wire_holder", modeled in this document).
Construction recipe (the document's own serialized feature program — sketch geometry with constraints, then the solid features built on it; lengths are millimeters unless a unit is written):

FEATURE [PartDesign::SubShapeBinder] Binder138
  BindCopyOnChange = 0
  BindMode = 0
  ClaimChildren = true
  Context = -> Body135 [Binder138.]
  Fuse = false
  MakeFace = true
  OffsetFill = false
  OffsetIntersection = false
  OffsetJoinType = 0
  OffsetOpenResult = false
  PartialLoad = false
  Relative = true
  Support = -> [Sketch237]
  _Version = 2
FEATURE [PartDesign::Pad] Pad038
  Direction = (0,0,1)
  Length = 10
  Length2 = 10
  Profile = -> Binder138 [Face1]
  Suppressed = false
  Type = 0
FEATURE [PartDesign::Boolean] Boolean042
  BaseFeature = -> Pad038
  Group = -> [Compound090]
  Suppressed = false
  Type = 1
  UsePlacement = false
FEATURE [PartDesign::Body] Body135  label="wire_holder"
  AllowCompound = false
  Group = -> [Binder138,Pad038,Boolean042]
  Origin = -> Origin113
  Tip = -> Boolean042
COMPONENT P19 — recipe-attached ("Body136", modeled in this document).
Construction recipe (the document's own serialized feature program — sketch geometry with constraints, then the solid features built on it; lengths are millimeters unless a unit is written):

FEATURE [Sketcher::SketchObject] Sketch238
  ArcFitTolerance = 0
  AttachmentSupport = -> [XY_Plane113]
  FullyConstrained = true
  MakeInternals = false
  MapMode = 5
  sketch-geometry (10):
    g0: LineSegment StartX=-10 StartY=-23.5 StartZ=0 EndX=10 EndY=-23.5 EndZ=0
    g1: LineSegment StartX=15 StartY=-18.5 StartZ=0 EndX=15 EndY=18.5 EndZ=0
    g2: LineSegment StartX=10 StartY=23.5 StartZ=0 EndX=-10 EndY=23.5 EndZ=0
    g3: LineSegment StartX=-15 StartY=18.5 StartZ=0 EndX=-15 EndY=-18.5 EndZ=0
    g4: ArcOfCircle CenterX=-10 CenterY=-18.5 CenterZ=0 NormalX=0 NormalY=0 NormalZ=1 AngleXU=0 Radius=5 StartAngle=3.14159 EndAngle=4.71239
    g5: ArcOfCircle CenterX=10 CenterY=-18.5 CenterZ=0 NormalX=0 NormalY=0 NormalZ=1 AngleXU=0 Radius=5 StartAngle=4.71239 EndAngle=6.28319
    g6: ArcOfCircle CenterX=10 CenterY=18.5 CenterZ=0 NormalX=0 NormalY=0 NormalZ=1 AngleXU=0 Radius=5 StartAngle=2.76279e-11 EndAngle=1.5708
    g7: ArcOfCircle CenterX=-10 CenterY=18.5 CenterZ=0 NormalX=0 NormalY=0 NormalZ=1 AngleXU=0 Radius=5 StartAngle=1.5708 EndAngle=3.14159
    g8: GeomPoint [constr] X=-15 Y=-23.5 Z=0
    g9: GeomPoint [constr] X=15 Y=23.5 Z=0
  constraints (23):
    c: Tangent(g0,g4) = -1.5708
    c: Tangent(g0,g5) = -1.5708
    c: Tangent(g1,g5) = -1.5708
    c: Tangent(g1,g6) = -1.5708
    c: Tangent(g2,g6) = -1.5708
    c: Tangent(g2,g7) = -1.5708
    c: Tangent(g3,g7) = -1.5708
    c: Tangent(g3,g4) = -1.5708
    c: Horizontal(g0)
    c: Horizontal(g2)
    c: Vertical(g1)
    c: Vertical(g3)
    c: Equal(g4,g5)
    c: Equal(g5,g6)
    c: Equal(g6,g7)
    c: PointOnObject(g8,g0)
    c: PointOnObject(g8,g3)
    c: PointOnObject(g9,g1)
    c: PointOnObject(g9,g2)
    c: Distance(g1,g3) = 30
    c: Distance(g0,g2) = 47
    c: Radius(g5) = 5
    c: Symmetric(g8,g9,g-1)
FEATURE [PartDesign::Pad] Pad039
  Direction = (0,0,1)
  Length = 1.5
  Length2 = 10
  Profile = -> Sketch238
  ReferenceAxis = -> Sketch238 [N_Axis]
  Suppressed = false
  Type = 0
FEATURE [PartDesign::SubShapeBinder] Binder139
  BindCopyOnChange = 0
  BindMode = 0
  ClaimChildren = true
  Fuse = false
  MakeFace = true
  OffsetFill = false
  OffsetIntersection = false
  OffsetJoinType = 0
  OffsetOpenResult = false
  PartialLoad = false
  Relative = false
  Support = -> [Sketch239]
  _Version = 2
FEATURE [PartDesign::Pocket] Pocket133
  BaseFeature = -> Pad039
  Direction = (0,0,-1)
  Length = 5
  Length2 = 5
  Midplane = true
  Profile = -> Binder139
  Suppressed = false
  Type = 1
FEATURE [PartDesign::Body] Body136
  AllowCompound = false
  Group = -> [Sketch238,Pad039,Binder139,Pocket133]
  Origin = -> Origin114
  Tip = -> Pocket133
COMPONENT P20 — recipe-attached ("Body139", modeled in this document).
Construction recipe (the document's own serialized feature program — sketch geometry with constraints, then the solid features built on it; lengths are millimeters unless a unit is written):

FEATURE [Sketcher::SketchObject] Sketch246
  ArcFitTolerance = 0
  AttachmentSupport = -> [XY_Plane116]
  FullyConstrained = true
  MakeInternals = false
  MapMode = 5
  sketch-geometry (7):
    g0: LineSegment StartX=7.50555 StartY=0 StartZ=0 EndX=3.75278 EndY=6.5 EndZ=0
    g1: LineSegment StartX=3.75278 StartY=6.5 StartZ=0 EndX=-3.75278 EndY=6.5 EndZ=0
    g2: LineSegment StartX=-3.75278 StartY=6.5 StartZ=0 EndX=-7.50555 EndY=4.3228e-12 EndZ=0
    g3: LineSegment StartX=-7.50555 StartY=4.3229e-12 StartZ=0 EndX=-3.75278 EndY=-6.5 EndZ=0
    g4: LineSegment StartX=-3.75278 StartY=-6.5 StartZ=0 EndX=3.75278 EndY=-6.5 EndZ=0
    g5: LineSegment StartX=3.75278 StartY=-6.5 StartZ=0 EndX=7.50555 EndY=0 EndZ=0
    g6: Circle [constr] CenterX=0 CenterY=0 CenterZ=0 NormalX=0 NormalY=0 NormalZ=1 AngleXU=0 Radius=7.50555
  constraints (16):
    c: Coincident(g0,g1)
    c: Coincident(g1,g2)
    c: Coincident(g2,g3)
    c: Coincident(g3,g4)
    c: Coincident(g4,g5)
    c: Coincident(g5,g0)
    c: Equal(g0, g1-g5) x5
    c: PointOnObject(g0,g6)
    c: PointOnObject(g1,g6)
    c: PointOnObject(g2,g6)
    c: PointOnObject(g3,g6)
    c: PointOnObject(g4,g6)
    c: PointOnObject(g5,g6)
    c: Coincident(g6,g-1)
    c: PointOnObject(g5,g-1)
    c: DistanceY(g4,g0) = 13
FEATURE [PartDesign::Pad] Pad042
  Direction = (0,0,1)
  Length = 5
  Length2 = 10
  Profile = -> Sketch246
  ReferenceAxis = -> Sketch246 [N_Axis]
  Suppressed = false
  Type = 0
FEATURE [Sketcher::SketchObject] Sketch247
  ArcFitTolerance = 0
  AttachmentSupport = -> [XY_Plane116]
  FullyConstrained = true
  MakeInternals = false
  MapMode = 5
  sketch-geometry (1):
    g0: Circle CenterX=0 CenterY=0 CenterZ=0 NormalX=0 NormalY=0 NormalZ=1 AngleXU=0 Radius=4.25
  constraints (2):
    c: Coincident(g0,g-1)
    c: Diameter(g0) = 8.5
FEATURE [PartDesign::Pad] Pad043
  BaseFeature = -> Pad042
  Direction = (0,0,1)
  Length = 20
  Length2 = 10
  Profile = -> Sketch247
  ReferenceAxis = -> Sketch247 [N_Axis]
  Suppressed = false
  Type = 0
FEATURE [PartDesign::Body] Body139
  AllowCompound = false
  Group = -> [Sketch246,Pad042,Sketch247,Pad043]
  Origin = -> Origin117
  Placement = pos=(60,0,0) rot=(0,0,1;0rad)
  Tip = -> Pad043
  expr: .Placement.Base.x = <<bottom_bearing_Sketch>>.Constraints.outer_r + 10 mm
COMPONENT P21 — recipe-attached ("pillar3", modeled in this document).
Construction recipe (the document's own serialized feature program — sketch geometry with constraints, then the solid features built on it; lengths are millimeters unless a unit is written):

FEATURE [PartDesign::SubShapeBinder] Binder141
  BindCopyOnChange = 0
  BindMode = 0
  ClaimChildren = true
  Fuse = false
  MakeFace = true
  OffsetFill = false
  OffsetIntersection = false
  OffsetJoinType = 0
  OffsetOpenResult = false
  PartialLoad = false
  Relative = false
  Support = -> [Sketch008]
  _Version = 2
  expr: Support = <<pillar_base_sketch>>._self
FEATURE [PartDesign::FeaturePython] BaseBend052  label="pillar3_BaseBend"  # WARN: FeaturePython — macro-defined, semantics opaque (R4)
  BendSide = 1
  BendSketch = -> Binder141
  MidPlane = false
  Reverse = false
  Suppressed = false
  length = 1684
  radius = 2
  thickness = 2
FEATURE [Sketcher::SketchObject] Sketch253
  ArcFitTolerance = 0
  AttachmentSupport = -> [YZ_Plane121]
  ExternalGeometry = -> [Binder141]
  FullyConstrained = true
  MakeInternals = false
  MapMode = 5
  Placement = pos=(0,0,0) rot=(0.57735,0.57735,0.57735;2.0944rad)
  sketch-geometry (3):
    g0: LineSegment StartX=14 StartY=0 StartZ=0 EndX=19 EndY=0 EndZ=0
    g1: LineSegment StartX=19 StartY=0 StartZ=0 EndX=19 EndY=5 EndZ=0
    g2: ArcOfCircle CenterX=14 CenterY=5 CenterZ=0 NormalX=0 NormalY=0 NormalZ=1 AngleXU=0 Radius=5 StartAngle=4.71239 EndAngle=6.28319
  constraints (7):
    c: PointOnObject(g0,g-3)
    c: Coincident(g0,g-3)
    c: Coincident(g1,g0)
    c: Vertical(g1)
    c: Tangent(g2,g1) = -1.5708
    c: Tangent(g2,g0) = -1.5708
    c: Radius(g2) = 5
FEATURE [PartDesign::Pocket] Pocket137
  BaseFeature = -> BaseBend052
  Direction = (-1,0,0)
  Length = 5
  Length2 = 5
  Midplane = true
  Profile = -> Sketch253
  ReferenceAxis = -> Sketch253 [N_Axis]
  Suppressed = false
  Type = 1
FEATURE [PartDesign::CoordinateSystem] Local_CS006  label="pillar3_base"
  AttacherType = Attacher::AttachEngine3D
  AttachmentSupport = -> [XY_Plane121]
  MapMode = 5
FEATURE [PartDesign::CoordinateSystem] Local_CS007  label="pillar3_hat_fix_Local_CS"
  AttacherType = Attacher::AttachEngine3D
  AttachmentOffset = pos=(0,2,1594) rot=(0,0,1;0rad)
  AttachmentSupport = -> [XY_Plane121]
  MapMode = 5
  Placement = pos=(0,2,1594) rot=(0,0,1;0rad)
  expr: AttachmentOffset = <<pillar3_hat_fix_placement>>.Placement
FEATURE [PartDesign::Plane] DatumPlane007
  AttachmentOffset = pos=(0,0,842) rot=(0,0,1;0rad)
  AttachmentSupport = -> [XY_Plane121]
  Length = 60
  MapMode = 5
  Placement = pos=(0,0,842) rot=(0,0,1;0rad)
  ResizeMode = 0
  Width = 60
  expr: .AttachmentOffset.Base.z = <<pillar3_BaseBend>>.length / 2
FEATURE [PartDesign::Mirrored] Mirrored020
  BaseFeature = -> Pocket137
  MirrorPlane = -> DatumPlane007
  Originals = -> [Pocket137]
  Suppressed = false
  TransformMode = 0
FEATURE [PartDesign::CoordinateSystem] Local_CS009  label="pillar3_dec_corner_LCS"
  AttacherType = Attacher::AttachEngine3D
  AttachmentOffset = pos=(0,0,470) rot=(0,0,1;0rad)
  AttachmentSupport = -> [XY_Plane121]
  MapMode = 5
  Placement = pos=(0,0,470) rot=(0,0,1;0rad)
  expr: AttachmentOffset = <<pillar3_dec_corner_placement>>.Placement
FEATURE [Sketcher::SketchObject] Sketch268
  ArcFitTolerance = 0
  AttachmentSupport = -> [YZ_Plane121]
  FullyConstrained = false
  MakeInternals = false
  MapMode = 5
  Placement = pos=(0,0,0) rot=(0.57735,0.57735,0.57735;2.0944rad)
  sketch-geometry (7):
    g0: Circle CenterX=11.5 CenterY=9 CenterZ=0 NormalX=0 NormalY=0 NormalZ=1 AngleXU=0 Radius=1.7
    g1: Circle CenterX=11.5 CenterY=40.3333 CenterZ=0 NormalX=0 NormalY=0 NormalZ=1 AngleXU=0 Radius=1.7
    g2: Circle CenterX=11.5 CenterY=71.6667 CenterZ=0 NormalX=0 NormalY=0 NormalZ=1 AngleXU=0 Radius=1.7
    g3: LineSegment [constr] StartX=11.5 StartY=9 StartZ=0 EndX=11.5 EndY=40.3333 EndZ=0
    g4: LineSegment [constr] StartX=11.5 StartY=40.3333 StartZ=0 EndX=11.5 EndY=71.6667 EndZ=0
    g5: Circle [constr] CenterX=11.5 CenterY=103 CenterZ=0 NormalX=0 NormalY=0 NormalZ=1 AngleXU=0 Radius=1.86607
    g6: LineSegment [constr] StartX=11.5 StartY=103 StartZ=0 EndX=11.5 EndY=71.6667 EndZ=0
  constraints (17):
    c: Equal(g0,g1)
    c: Equal(g0,g2)
    c: Diameter(g0) = 3.4
    c: Coincident(g3,g0)
    c: Coincident(g3,g1)
    c: Coincident(g3,g4)
    c: Coincident(g4,g2)
    c: Vertical(g4)
    c: Vertical(g3)
    c: Equal(g3,g4)
    c: Coincident(g6,g5)
    c: Coincident(g6,g2)
    c: Vertical(g6)
    c: DistanceY(g0) = 9
    c: DistanceX(g0) = 11.5
    c: Equal(g6,g4)
    c: DistanceY(g5) = 103
FEATURE [PartDesign::CoordinateSystem] Local_CS047  label="pillar3_bottom_LCS"
  AttacherType = Attacher::AttachEngine3D
  AttachmentOffset = pos=(18.3,4,0) rot=(0,0,1;1.5708rad)
  AttachmentSupport = -> [XY_Plane121]
  MapMode = 5
  Placement = pos=(18.3,4,0) rot=(0,0,1;1.5708rad)
FEATURE [PartDesign::Boolean] Boolean049
  BaseFeature = -> Mirrored020
  Group = -> [Compound099]
  Suppressed = false
  Type = 1
  UsePlacement = true
FEATURE [PartDesign::Pocket] Pocket144
  BaseFeature = -> Boolean049
  Direction = (-1,0,0)
  Length = 5
  Length2 = 5
  Midplane = true
  Profile = -> Sketch268
  ReferenceAxis = -> Sketch268 [N_Axis]
  Suppressed = false
  Type = 1
FEATURE [PartDesign::Body] Body141  label="pillar3"
  AllowCompound = false
  Group = -> [Binder141,BaseBend052,Sketch253,Pocket137,Local_CS006,Local_CS007,DatumPlane007,Mirrored020,Local_CS009,Boolean049,Sketch268,Local_CS047,Pocket144]
  Origin = -> Origin122
  Tip = -> Pocket144
COMPONENT P22 — recipe-attached ("hat3_base", modeled in this document).
Construction recipe (the document's own serialized feature program — sketch geometry with constraints, then the solid features built on it; lengths are millimeters unless a unit is written):

FEATURE [PartDesign::SubShapeBinder] Binder142
  BindCopyOnChange = 0
  BindMode = 0
  ClaimChildren = true
  Context = -> Body142 [Binder142.]
  Fuse = false
  MakeFace = true
  OffsetFill = false
  OffsetIntersection = false
  OffsetJoinType = 0
  OffsetOpenResult = false
  PartialLoad = false
  Relative = true
  Support = -> [Connect005]
  _Version = 2
FEATURE [PartDesign::Pad] Pad045
  Direction = (0,0,1)
  Length = 3
  Length2 = 10
  Profile = -> Binder142
  Refine = true
  Suppressed = false
  Type = 0
FEATURE [PartDesign::CoordinateSystem] Local_CS037  label="hat3_bottom_bottom_LCS"
  AttacherType = Attacher::AttachEngine3D
  AttachmentSupport = -> [XY_Plane122]
  MapMode = 2
FEATURE [PartDesign::CoordinateSystem] Local_CS038  label="hat3_bottom_top_LCS"
  AttacherType = Attacher::AttachEngine3D
  AttachmentOffset = pos=(0,0,3) rot=(0,0,1;0rad)
  AttachmentSupport = -> [XY_Plane122]
  MapMode = 5
  Placement = pos=(0,0,3) rot=(0,0,1;0rad)
FEATURE [PartDesign::Boolean] Boolean050
  BaseFeature = -> Pad045
  Group = -> [Compound102]
  Suppressed = false
  Type = 1
  UsePlacement = true
FEATURE [PartDesign::Body] Body142  label="hat3_base"
  AllowCompound = false
  Group = -> [Binder142,Pad045,Boolean050,Local_CS037,Local_CS038]
  Origin = -> Origin123
  Tip = -> Boolean050
COMPONENT P23 — recipe-attached ("hat3_cap", modeled in this document).
Construction recipe (the document's own serialized feature program — sketch geometry with constraints, then the solid features built on it; lengths are millimeters unless a unit is written):

FEATURE [PartDesign::SubShapeBinder] Binder146
  BindCopyOnChange = 0
  BindMode = 0
  ClaimChildren = true
  Context = -> Body143 [Binder146.]
  Fuse = false
  MakeFace = true
  OffsetFill = false
  OffsetIntersection = false
  OffsetJoinType = 0
  OffsetOpenResult = false
  PartialLoad = false
  Relative = false
  Support = -> [Connect007]
  _Version = 2
FEATURE [PartDesign::CoordinateSystem] Local_CS044  label="hat3_cap_bottom_LCS"
  AttacherType = Attacher::AttachEngine3D
  AttachmentSupport = -> [XY_Plane123]
  MapMode = 5
FEATURE [PartDesign::CoordinateSystem] Local_CS045  label="hat3_cap_top_LCS"
  AttacherType = Attacher::AttachEngine3D
  AttachmentOffset = pos=(0,0,3) rot=(0,0,1;0rad)
  AttachmentSupport = -> [XY_Plane123]
  MapMode = 5
  Placement = pos=(0,0,3) rot=(0,0,1;0rad)
FEATURE [Sketcher::SketchObject] Sketch281
  ArcFitTolerance = 0
  AttachmentSupport = -> [XY_Plane123]
  FullyConstrained = true
  MakeInternals = false
  MapMode = 5
  sketch-geometry (2):
    g0: Circle CenterX=100 CenterY=-90 CenterZ=0 NormalX=0 NormalY=0 NormalZ=1 AngleXU=0 Radius=15
    g1: Circle CenterX=-100 CenterY=-90 CenterZ=0 NormalX=0 NormalY=0 NormalZ=1 AngleXU=0 Radius=15
  constraints (5):
    c: Equal(g1,g0)
    c: Diameter(g0) = 30
    c: DistanceX(g0) = 100
    c: DistanceY(g0) = -90
    c: Symmetric(g1,g0,g-2)
FEATURE [Sketcher::SketchObject] Sketch285
  ArcFitTolerance = 0
  AttachmentOffset = pos=(0,370,0) rot=(0,0,1;0rad)
  AttachmentSupport = -> [XY_Plane123]
  FullyConstrained = true
  MakeInternals = false
  MapMode = 5
  Placement = pos=(0,370,0) rot=(0,0,1;0rad)
  sketch-geometry (1):
    g0: Circle CenterX=0 CenterY=0 CenterZ=0 NormalX=0 NormalY=0 NormalZ=1 AngleXU=0 Radius=1.7
  constraints (2):
    c: Coincident(g0,g-1)
    c: Diameter(g0) = 3.4
FEATURE [PartDesign::FeaturePython] BaseBend059  # WARN: FeaturePython — macro-defined, semantics opaque (R4)
  BendSide = 0
  BendSketch = -> Binder146
  MidPlane = false
  Reverse = false
  Suppressed = false
  length = 100
  radius = 0.1
  thickness = 0.3
FEATURE [PartDesign::Pocket] Pocket147
  BaseFeature = -> BaseBend059
  Direction = (0,0,-1)
  Length = 5
  Length2 = 5
  Profile = -> Sketch285
  ReferenceAxis = -> Sketch285 [N_Axis]
  Reversed = true
  Suppressed = false
  Type = 0
FEATURE [PartDesign::PolarPattern] PolarPattern012
  Angle = 360
  Axis = -> Z_Axis123
  BaseFeature = -> Pocket147
  Mode = 0
  Occurrences = 3
  Offset = 120
  Originals = -> [Pocket147]
  Suppressed = false
  TransformMode = 0
FEATURE [PartDesign::Boolean] Boolean061
  BaseFeature = -> PolarPattern012
  Group = -> [Compound115]
  Suppressed = false
  Type = 1
  UsePlacement = true
FEATURE [PartDesign::FeaturePython] Bend031  # WARN: FeaturePython — macro-defined, semantics opaque (R4)
  AutoMiter = true
  BaseFeature = -> Boolean061
  BendType = 0
  LengthList = [29]
  LengthSpec = 1
  NonperforationMaxLength = 5
  Perforate = false
  PerforationAngle = 0
  PerforationInitialLength = 5
  PerforationMaxLength = 5
  ReliefFactor = 0.7
  Suppressed = false
  UseReliefFactor = false
  angle = 90
  baseObject = -> Boolean061 [Edge41,Edge43]
  bendAList = [90]
  extend1 = 0
  extend2 = 0
  gap1 = 3.2
  gap2 = 3.2
  invert = false
  kfactor = 0.5
  length = 29
  maxExtendDist = 5
  minGap = 0.2
  minReliefGap = 1
  miterangle1 = 0
  miterangle2 = 0
  offset = 0
  radius = 0.1
  reliefType = 0
  reliefd = 1
  reliefw = 0.8
  sketchflip = false
  sketchinvert = false
  unfold = false
  expr: radius = BaseBend059.radius
FEATURE [PartDesign::Boolean] Boolean062
  BaseFeature = -> Bend031
  Group = -> [Fusion010]
  Suppressed = false
  Type = 1
  UsePlacement = true
FEATURE [PartDesign::Body] Body143  label="hat3_cap"
  AllowCompound = false
  Group = -> [Binder146,Local_CS044,Local_CS045,Sketch281,Sketch285,BaseBend059,Pocket147,PolarPattern012,Boolean061,Bend031,Boolean062]
  Origin = -> Origin124
  Tip = -> Boolean062
COMPONENT P24 — recipe-attached ("pillar3_hat_fix", modeled in this document).
Construction recipe (the document's own serialized feature program — sketch geometry with constraints, then the solid features built on it; lengths are millimeters unless a unit is written):

FEATURE [PartDesign::SubShapeBinder] Binder143
  BindCopyOnChange = 0
  BindMode = 0
  ClaimChildren = true
  Fuse = false
  MakeFace = true
  OffsetFill = false
  OffsetIntersection = false
  OffsetJoinType = 0
  OffsetOpenResult = false
  PartialLoad = false
  Placement = pos=(0,0,0) rot=(0,-1,0;1.5708rad)
  Relative = false
  Support = -> [Sketch251]
  _Version = 2
FEATURE [PartDesign::FeaturePython] BaseBend053  label="pillar3_hat_fix_BaseBend"  # WARN: FeaturePython — macro-defined, semantics opaque (R4)
  BendSide = 1
  BendSketch = -> Binder143
  MidPlane = true
  Reverse = false
  Suppressed = false
  length = 28.6
  radius = 2
  thickness = 1.5
  expr: length = <<pillar_base_sketch>>.Constraints.width - 8 mm
FEATURE [Sketcher::SketchObject] Sketch256
  ArcFitTolerance = 0
  AttachmentSupport = -> [XY_Plane124]
  ExternalGeometry = -> [Binder143]
  FullyConstrained = true
  MakeInternals = false
  MapMode = 5
  expr: Constraints[12] = <<pillar3_hat_fix_BaseBend>>.length
  sketch-geometry (6):
    g0: LineSegment StartX=9.3 StartY=70 StartZ=0 EndX=14.3 EndY=70 EndZ=0
    g1: LineSegment StartX=14.3 StartY=70 StartZ=0 EndX=14.3 EndY=65 EndZ=0
    g2: LineSegment StartX=-14.3 StartY=65 StartZ=0 EndX=-14.3 EndY=70 EndZ=0
    g3: LineSegment StartX=-14.3 StartY=70 StartZ=0 EndX=-9.3 EndY=70 EndZ=0
    g4: ArcOfCircle CenterX=9.3 CenterY=65 CenterZ=0 NormalX=0 NormalY=0 NormalZ=1 AngleXU=0 Radius=5 StartAngle=4e-16 EndAngle=1.5708
    g5: ArcOfCircle CenterX=-9.3 CenterY=65 CenterZ=0 NormalX=0 NormalY=0 NormalZ=1 AngleXU=0 Radius=5 StartAngle=1.5708 EndAngle=3.14159
  constraints (15):
    c: Coincident(g0,g1)
    c: Coincident(g2,g3)
    c: Tangent(g5,g2) = 1.5708
    c: Tangent(g5,g3) = 1.5708
    c: Tangent(g4,g1) = 1.5708
    c: Tangent(g4,g0) = 1.5708
    c: Equal(g4,g5)
    c: Radius(g5) = 5
    c: Parallel(g1,g-3)
    c: Perpendicular(g-3,g0)
    c: Perpendicular(g-3,g3)
    c: Parallel(g2,g-3)
    c: DistanceX(g2,g0) = 28.6
    c: Horizontal(g2,g0)
    c: Symmetric(g0,g2,g-3)
FEATURE [Sketcher::SketchObject] Sketch257
  ArcFitTolerance = 0
  AttachmentOffset = pos=(0,0,4) rot=(0,0,1;0rad)
  AttachmentSupport = -> [XY_Plane124]
  ExternalGeometry = -> [Binder143]
  FullyConstrained = true
  MakeInternals = false
  MapMode = 5
  Placement = pos=(0,0,4) rot=(0,0,1;0rad)
  expr: Constraints[13] = <<pillar3_hat_fix_BaseBend>>.length
  sketch-geometry (6):
    g0: LineSegment StartX=9.3 StartY=30 StartZ=0 EndX=14.3 EndY=30 EndZ=0
    g1: LineSegment StartX=14.3 StartY=30 StartZ=0 EndX=14.3 EndY=25 EndZ=0
    g2: LineSegment StartX=-14.3 StartY=25 StartZ=0 EndX=-14.3 EndY=30 EndZ=0
    g3: LineSegment StartX=-14.3 StartY=30 StartZ=0 EndX=-9.3 EndY=30 EndZ=0
    g4: ArcOfCircle CenterX=9.3 CenterY=25 CenterZ=0 NormalX=0 NormalY=0 NormalZ=1 AngleXU=0 Radius=5 StartAngle=3e-16 EndAngle=1.5708
    g5: ArcOfCircle CenterX=-9.3 CenterY=25 CenterZ=0 NormalX=0 NormalY=0 NormalZ=1 AngleXU=0 Radius=5 StartAngle=1.5708 EndAngle=3.14159
  constraints (15):
    c: Coincident(g0,g1)
    c: Coincident(g2,g3)
    c: Tangent(g5,g2) = 1.5708
    c: Tangent(g5,g3) = 1.5708
    c: Tangent(g4,g1) = 1.5708
    c: Tangent(g4,g0) = 1.5708
    c: Equal(g4,g5)
    c: Radius(g4) = 5
    c: Symmetric(g2,g0,g-3)
    c: Parallel(g2,g-3)
    c: Parallel(g-3,g1)
    c: Perpendicular(g0,g1)
    c: Horizontal(g0,g-3)
    c: DistanceX(g2,g0) = 28.6
    c: Perpendicular(g-3,g3)
FEATURE [PartDesign::CoordinateSystem] Local_CS005
  AttacherType = Attacher::AttachEngine3D
  AttachmentSupport = -> [XY_Plane124]
  MapMode = 5
FEATURE [Sketcher::SketchObject] Sketch265
  ArcFitTolerance = 0
  AttachmentSupport = -> [XY_Plane124]
  FullyConstrained = true
  MakeInternals = false
  MapMode = 5
  expr: Constraints[4] = <<pillar3_hat_fix_BaseBend>>.length / 2
  sketch-geometry (8):
    g0: LineSegment StartX=11.3 StartY=14 StartZ=0 EndX=10 EndY=14 EndZ=0
    g1: ArcOfCircle CenterX=10 CenterY=9 CenterZ=0 NormalX=0 NormalY=0 NormalZ=1 AngleXU=0 Radius=5 StartAngle=1.5708 EndAngle=3.14159
    g2: LineSegment StartX=5 StartY=9 StartZ=0 EndX=5 EndY=1 EndZ=0
    g3: LineSegment StartX=14.3 StartY=17 StartZ=0 EndX=14.3 EndY=-7 EndZ=0
    g4: ArcOfCircle CenterX=10 CenterY=1 CenterZ=0 NormalX=0 NormalY=0 NormalZ=1 AngleXU=0 Radius=5 StartAngle=3.14159 EndAngle=4.71239
    g5: ArcOfCircle CenterX=11.3 CenterY=-7 CenterZ=0 NormalX=0 NormalY=0 NormalZ=1 AngleXU=0 Radius=3 StartAngle=-7.46e-14 EndAngle=1.5708
    g6: ArcOfCircle CenterX=11.3 CenterY=17 CenterZ=0 NormalX=0 NormalY=0 NormalZ=1 AngleXU=0 Radius=3 StartAngle=4.71239 EndAngle=6.28319
    g7: LineSegment StartX=10 StartY=-4 StartZ=0 EndX=11.3 EndY=-4 EndZ=0
  constraints (20):
    c: Horizontal(g0)
    c: Vertical(g2)
    c: Vertical(g3)
    c: Radius(g1) = 5
    c: DistanceX(g3) = 14.3
    c: Tangent(g1,g0) = -1.5708
    c: Tangent(g2,g1) = -1.5708
    c: DistanceX(g2) = 5
    c: Tangent(g0,g6) = 1.5708
    c: Tangent(g3,g6) = 1.5708
    c: Horizontal(g7)
    c: Tangent(g3,g5) = 1.5708
    c: Tangent(g4,g2) = -1.5708
    c: Tangent(g7,g4) = -1.5708
    c: Tangent(g7,g5) = 1.5708
    c: Radius(g6) = 3
    c: Equal(g6,g5)
    c: Equal(g4,g1)
    c: DistanceY(g0) = 14
    c: DistanceY(g4) = -4
FEATURE [PartDesign::FeaturePython] SketchOnSheet  # WARN: FeaturePython — macro-defined, semantics opaque (R4)
  BaseFeature = -> BaseBend053
  Sketch = -> Sketch265
  Suppressed = false
  baseObject = -> BaseBend053 [Face22]
  kfactor = 0.5
FEATURE [PartDesign::Pocket] Pocket138
  BaseFeature = -> SketchOnSheet
  Direction = (0,0,-1)
  Length = 5
  Length2 = 5
  Profile = -> Sketch256
  ReferenceAxis = -> Sketch256 [N_Axis]
  Reversed = true
  Suppressed = false
  Type = 0
FEATURE [PartDesign::Pocket] Pocket139
  BaseFeature = -> Pocket138
  Direction = (0,0,-1)
  Length = 5
  Length2 = 5
  Profile = -> Sketch257
  ReferenceAxis = -> Sketch257 [N_Axis]
  Reversed = true
  Suppressed = false
  Type = 1
FEATURE [PartDesign::Boolean] Boolean046
  BaseFeature = -> Pocket139
  Group = -> [Compound094]
  Suppressed = false
  Type = 1
  UsePlacement = true
FEATURE [PartDesign::Body] Body144  label="pillar3_hat_fix"
  AllowCompound = false
  Group = -> [Binder143,BaseBend053,Sketch256,Sketch257,SketchOnSheet,Pocket138,Pocket139,Local_CS005,Boolean046,Sketch265]
  Origin = -> Origin125
  Tip = -> Boolean046
COMPONENT P25 — recipe-attached ("pilllar3_dec_corner", modeled in this document).
Construction recipe (the document's own serialized feature program — sketch geometry with constraints, then the solid features built on it; lengths are millimeters unless a unit is written):

FEATURE [PartDesign::SubShapeBinder] Binder144
  BindCopyOnChange = 0
  BindMode = 0
  ClaimChildren = true
  Context = -> Body145 [Binder144.]
  Fuse = false
  MakeFace = true
  OffsetFill = false
  OffsetIntersection = false
  OffsetJoinType = 0
  OffsetOpenResult = false
  PartialLoad = false
  Relative = true
  Support = -> [Sketch056]
  _Version = 2
  expr: Support = <<pillar_dec_corner_base_sketch>>._self
FEATURE [PartDesign::FeaturePython] BaseBend054  label="pillar3_dec_corner_BaseBend"  # WARN: FeaturePython — macro-defined, semantics opaque (R4)
  BendSide = 0
  BendSketch = -> Binder144
  MidPlane = false
  Reverse = false
  Suppressed = false
  length = 1214
  radius = 2
  thickness = 0.5
  expr: length = <<pillar3_BaseBend>>.length - <<pillar3_dec_corner_placement>>.Placement.Base.z
FEATURE [Sketcher::SketchObject] Sketch260
  ArcFitTolerance = 0
  AttachmentSupport = -> [XZ_Plane125]
  ExternalGeometry = -> [Binder144]
  FullyConstrained = true
  MakeInternals = false
  MapMode = 5
  Placement = pos=(0,0,0) rot=(1,0,0;1.5708rad)
  sketch-geometry (3):
    g0: LineSegment StartX=13.3 StartY=0 StartZ=0 EndX=18.3 EndY=-3e-16 EndZ=0
    g1: LineSegment StartX=18.3 StartY=-3e-16 StartZ=0 EndX=18.3 EndY=5 EndZ=0
    g2: ArcOfCircle CenterX=13.3 CenterY=5 CenterZ=0 NormalX=0 NormalY=0 NormalZ=1 AngleXU=0 Radius=5 StartAngle=4.71239 EndAngle=6.28319
  constraints (7):
    c: PointOnObject(g0,g-3)
    c: Coincident(g0,g-3)
    c: Coincident(g0,g1)
    c: Vertical(g1)
    c: Tangent(g2,g1) = -1.5708
    c: Tangent(g2,g0) = -1.5708
    c: Radius(g2) = 5
FEATURE [Sketcher::SketchObject] Sketch261
  ArcFitTolerance = 0
  AttachmentSupport = -> [YZ_Plane125]
  ExternalGeometry = -> [Binder144]
  FullyConstrained = true
  MakeInternals = false
  MapMode = 5
  Placement = pos=(0,0,0) rot=(0.57735,0.57735,0.57735;2.0944rad)
  sketch-geometry (3):
    g0: LineSegment StartX=14 StartY=9e-16 StartZ=0 EndX=19 EndY=0 EndZ=0
    g1: LineSegment StartX=19 StartY=0 StartZ=0 EndX=19 EndY=5 EndZ=0
    g2: ArcOfCircle CenterX=14 CenterY=5 CenterZ=0 NormalX=0 NormalY=0 NormalZ=1 AngleXU=0 Radius=5 StartAngle=4.71239 EndAngle=6.28319
  constraints (7):
    c: PointOnObject(g0,g-3)
    c: Coincident(g0,g-3)
    c: Coincident(g0,g1)
    c: Vertical(g1)
    c: Tangent(g2,g1) = -1.5708
    c: Tangent(g2,g0) = -1.5708
    c: Radius(g2) = 5
FEATURE [PartDesign::Pocket] Pocket140
  BaseFeature = -> BaseBend054
  Direction = (0,1,-2e-16)
  Length = 5
  Length2 = 5
  Midplane = true
  Profile = -> Sketch260
  ReferenceAxis = -> Sketch260 [N_Axis]
  Suppressed = false
  Type = 1
FEATURE [PartDesign::Pocket] Pocket141
  BaseFeature = -> Pocket140
  Direction = (-1,0,0)
  Length = 5
  Length2 = 5
  Midplane = true
  Profile = -> Sketch261
  ReferenceAxis = -> Sketch261 [N_Axis]
  Suppressed = false
  Type = 1
FEATURE [PartDesign::Plane] DatumPlane008
  AttachmentOffset = pos=(0,0,607) rot=(0,0,1;0rad)
  AttachmentSupport = -> [XY_Plane125]
  Length = 60
  MapMode = 5
  Placement = pos=(0,0,607) rot=(0,0,1;0rad)
  ResizeMode = 0
  Width = 60
  expr: .AttachmentOffset.Base.z = <<pillar3_dec_corner_BaseBend>>.length / 2
FEATURE [PartDesign::Mirrored] Mirrored021
  BaseFeature = -> Pocket141
  MirrorPlane = -> DatumPlane008
  Originals = -> [Pocket140,Pocket141]
  Suppressed = false
  TransformMode = 0
FEATURE [PartDesign::CoordinateSystem] Local_CS008  label="pilllar3_dec_corner_base_local_cs"
  AttacherType = Attacher::AttachEngine3D
  AttachmentSupport = -> [XY_Plane125]
  MapMode = 5
FEATURE [PartDesign::Boolean] Boolean048
  BaseFeature = -> Mirrored021
  Group = -> [Compound098]
  Suppressed = false
  Type = 1
  UsePlacement = true
FEATURE [PartDesign::Body] Body145  label="pilllar3_dec_corner"
  AllowCompound = false
  Group = -> [Binder144,BaseBend054,Sketch260,Sketch261,Pocket140,Pocket141,DatumPlane008,Mirrored021,Local_CS008,Boolean048]
  Origin = -> Origin126
  Tip = -> Boolean048
COMPONENT P26 — recipe-attached ("hat3_plexiglass", modeled in this document).
Construction recipe (the document's own serialized feature program — sketch geometry with constraints, then the solid features built on it; lengths are millimeters unless a unit is written):

FEATURE [PartDesign::SubShapeBinder] Binder145
  BindCopyOnChange = 0
  BindMode = 0
  ClaimChildren = true
  Context = -> Body146 [Binder145.]
  Fuse = false
  MakeFace = true
  OffsetFill = false
  OffsetIntersection = false
  OffsetJoinType = 0
  OffsetOpenResult = false
  PartialLoad = false
  Relative = false
  Support = -> [Connect006]
  _Version = 2
FEATURE [PartDesign::FeaturePython] BaseBend055  # WARN: FeaturePython — macro-defined, semantics opaque (R4)
  BendSide = 1
  BendSketch = -> Binder145
  MidPlane = false
  Reverse = false
  Suppressed = false
  length = 100
  radius = 1
  thickness = 1.5
FEATURE [PartDesign::FeaturePython] Extend002  # WARN: FeaturePython — macro-defined, semantics opaque (R4)
  BaseFeature = -> BaseBend055
  Offset = 0.02
  Refine = true
  Suppressed = false
  UseSubtraction = false
  baseObject = -> BaseBend055 [Face1]
  gap1 = 0
  gap2 = 0
  length = 0
FEATURE [PartDesign::Boolean] Boolean047
  BaseFeature = -> Extend002
  Group = -> [Compound096]
  Suppressed = false
  Type = 1
  UsePlacement = true
FEATURE [Sketcher::SketchObject] Sketch278
  ArcFitTolerance = 0
  AttachmentOffset = pos=(0,0,0) rot=(0,1,0;1.5708rad)
  AttachmentSupport = -> [Binder145]
  FullyConstrained = true
  MakeInternals = false
  MapMode = 7
  Placement = pos=(113.449,65.5,0) rot=(-0.774597,0.447214,0.447214;4.45971rad)
  sketch-geometry (1):
    g0: Circle CenterX=0 CenterY=22 CenterZ=0 NormalX=0 NormalY=0 NormalZ=1 AngleXU=0 Radius=1.7
  constraints (3):
    c: PointOnObject(g0,g-2)
    c: Diameter(g0) = 3.4
    c: DistanceY(g0) = 22
FEATURE [PartDesign::Pocket] Pocket146
  BaseFeature = -> Boolean047
  Direction = (0.866025,0.5,0)
  Length = 5
  Length2 = 5
  Midplane = true
  Profile = -> Sketch278
  ReferenceAxis = -> Sketch278 [N_Axis]
  Suppressed = false
  Type = 1
FEATURE [PartDesign::CoordinateSystem] Local_CS050  label="hat3_plexiglass_LCS"
  AttacherType = Attacher::AttachEngine3D
  AttachmentSupport = -> [XY_Plane126]
  MapMode = 5
FEATURE [PartDesign::Body] Body146  label="hat3_plexiglass"
  AllowCompound = false
  Group = -> [Binder145,BaseBend055,Extend002,Boolean047,Sketch278,Pocket146,Local_CS050]
  Origin = -> Origin127
  Tip = -> Pocket146
COMPONENT P27 — recipe-attached ("pilllar3_dec_corner_mirror", modeled in this document).
Construction recipe (the document's own serialized feature program — sketch geometry with constraints, then the solid features built on it; lengths are millimeters unless a unit is written):

FEATURE [PartDesign::SubShapeBinder] Binder148
  BindCopyOnChange = 0
  BindMode = 0
  ClaimChildren = true
  Context = -> Body147 [Binder148.]
  Fuse = false
  MakeFace = true
  OffsetFill = false
  OffsetIntersection = false
  OffsetJoinType = 0
  OffsetOpenResult = false
  PartialLoad = false
  Relative = false
  Support = -> [Part__Mirroring037]
  _Version = 2
FEATURE [PartDesign::FeaturePython] BaseBend056  label="pilllar3_dec_corner_mirror_BaseBend"  # WARN: FeaturePython — macro-defined, semantics opaque (R4)
  BendSide = 1
  BendSketch = -> Binder148
  MidPlane = false
  Reverse = false
  Suppressed = false
  length = 1214
  radius = 2
  thickness = 0.5
  expr: length = <<pillar3_dec_corner_BaseBend>>.length
  expr: radius = <<pillar3_dec_corner_BaseBend>>.radius
  expr: thickness = <<pillar3_dec_corner_BaseBend>>.thickness
FEATURE [Sketcher::SketchObject] Sketch266
  ArcFitTolerance = 0
  AttachmentSupport = -> [XZ_Plane127]
  ExternalGeometry = -> [Binder148]
  FullyConstrained = true
  MakeInternals = false
  MapMode = 5
  Placement = pos=(0,0,0) rot=(1,0,0;1.5708rad)
  sketch-geometry (3):
    g0: ArcOfCircle CenterX=-13.3 CenterY=5 CenterZ=0 NormalX=0 NormalY=0 NormalZ=1 AngleXU=0 Radius=5 StartAngle=3.14159 EndAngle=4.71239
    g1: LineSegment StartX=-18.3 StartY=5 StartZ=0 EndX=-18.3 EndY=0 EndZ=0
    g2: LineSegment StartX=-18.3 StartY=0 StartZ=0 EndX=-13.3 EndY=0 EndZ=0
  constraints (7):
    c: PointOnObject(g0,g-3)
    c: Coincident(g1,g2)
    c: Vertical(g1)
    c: Coincident(g1,g-3)
    c: Tangent(g0,g1) = -1.5708
    c: Radius(g0) = 5
    c: Tangent(g2,g0) = -1.5708
FEATURE [Sketcher::SketchObject] Sketch267
  ArcFitTolerance = 0
  AttachmentSupport = -> [YZ_Plane127]
  ExternalGeometry = -> [Binder148]
  FullyConstrained = true
  MakeInternals = false
  MapMode = 5
  Placement = pos=(0,0,0) rot=(0.57735,0.57735,0.57735;2.0944rad)
  sketch-geometry (3):
    g0: LineSegment StartX=14 StartY=6.04e-13 StartZ=0 EndX=19 EndY=0 EndZ=0
    g1: LineSegment StartX=19 StartY=0 StartZ=0 EndX=19 EndY=5 EndZ=0
    g2: ArcOfCircle CenterX=14 CenterY=5 CenterZ=0 NormalX=0 NormalY=0 NormalZ=1 AngleXU=0 Radius=5 StartAngle=4.71239 EndAngle=6.28319
  constraints (7):
    c: PointOnObject(g0,g-1)
    c: Coincident(g0,g1)
    c: Vertical(g1)
    c: Coincident(g0,g-3)
    c: Tangent(g2,g1) = -1.5708
    c: Tangent(g2,g0) = -1.5708
    c: Radius(g2) = 5
FEATURE [PartDesign::Pocket] Pocket142
  BaseFeature = -> BaseBend056
  Direction = (0,1,-2e-16)
  Length = 5
  Length2 = 5
  Midplane = true
  Profile = -> Sketch266
  ReferenceAxis = -> Sketch266 [N_Axis]
  Suppressed = false
  Type = 1
FEATURE [PartDesign::Pocket] Pocket143
  BaseFeature = -> Pocket142
  Direction = (-1,0,0)
  Length = 5
  Length2 = 5
  Midplane = true
  Profile = -> Sketch267
  ReferenceAxis = -> Sketch267 [N_Axis]
  Suppressed = false
  Type = 1
FEATURE [PartDesign::Plane] DatumPlane009
  AttachmentOffset = pos=(0,0,607) rot=(0,0,1;0rad)
  AttachmentSupport = -> [XY_Plane127]
  Length = 60
  MapMode = 5
  Placement = pos=(0,0,607) rot=(0,0,1;0rad)
  ResizeMode = 0
  Width = 60
  expr: .AttachmentOffset.Base.z = <<pilllar3_dec_corner_mirror_BaseBend>>.length / 2
FEATURE [PartDesign::Mirrored] Mirrored022
  BaseFeature = -> Pocket143
  MirrorPlane = -> DatumPlane009
  Originals = -> [Pocket142,Pocket143]
  Suppressed = false
  TransformMode = 0
FEATURE [PartDesign::Boolean] Boolean051
  BaseFeature = -> Mirrored022
  Group = -> [Compound103]
  Suppressed = false
  Type = 1
  UsePlacement = true
FEATURE [PartDesign::CoordinateSystem] Local_CS043
  AttacherType = Attacher::AttachEngine3D
  AttachmentSupport = -> [XY_Plane127]
  MapMode = 5
FEATURE [PartDesign::Body] Body147  label="pilllar3_dec_corner_mirror"
  AllowCompound = false
  Group = -> [Binder148,BaseBend056,Sketch266,Sketch267,Pocket142,Pocket143,DatumPlane009,Mirrored022,Boolean051,Local_CS043]
  Origin = -> Origin128
  Tip = -> Boolean051
COMPONENT P28 — recipe-attached ("basement_v4_bottom_amplifier", modeled in this document).
Construction recipe (the document's own serialized feature program — sketch geometry with constraints, then the solid features built on it; lengths are millimeters unless a unit is written):

FEATURE [PartDesign::SubShapeBinder] Binder150
  BindCopyOnChange = 0
  BindMode = 0
  ClaimChildren = true
  Context = -> Body148 [Binder150.]
  Fuse = false
  MakeFace = true
  OffsetFill = false
  OffsetIntersection = false
  OffsetJoinType = 0
  OffsetOpenResult = false
  PartialLoad = false
  Relative = false
  Support = -> [Connect008]
  _Version = 2
FEATURE [PartDesign::Pad] Pad047
  Direction = (0,0,1)
  Length = 18
  Length2 = 10
  Profile = -> Binder150
  Suppressed = false
  Type = 0
FEATURE [PartDesign::Boolean] Boolean053
  BaseFeature = -> Pad047
  Group = -> [Compound106]
  Suppressed = false
  Type = 1
  UsePlacement = true
FEATURE [PartDesign::Body] Body148  label="basement_v4_bottom_amplifier"
  AllowCompound = false
  Group = -> [Binder150,Pad047,Boolean053]
  Origin = -> Origin129
  Tip = -> Boolean053
COMPONENT P29 — recipe-attached ("basement_v4_bottom", modeled in this document).
Construction recipe (the document's own serialized feature program — sketch geometry with constraints, then the solid features built on it; lengths are millimeters unless a unit is written):

FEATURE [PartDesign::SubShapeBinder] Binder151
  BindCopyOnChange = 0
  BindMode = 0
  ClaimChildren = false
  Context = -> Body149 [Binder151.]
  Fuse = false
  MakeFace = true
  OffsetFill = false
  OffsetIntersection = false
  OffsetJoinType = 0
  OffsetOpenResult = false
  PartialLoad = false
  Relative = true
  Support = -> [Array002]
  _Version = 2
  expr: Support = <<basement_bottom_2d>>._self
FEATURE [PartDesign::Pad] Pad048
  Direction = (0,0,1)
  Length = 18
  Length2 = 10
  Profile = -> Binder151
  Suppressed = false
  Type = 0
FEATURE [PartDesign::Boolean] Boolean054
  BaseFeature = -> Pad048
  Group = -> [Compound107]
  Suppressed = false
  Type = 1
  UsePlacement = true
FEATURE [PartDesign::Body] Body149  label="basement_v4_bottom"
  AllowCompound = false
  Group = -> [Binder151,Pad048,Boolean054]
  Origin = -> Origin130
  Tip = -> Boolean054
COMPONENT P30 — recipe-attached ("basement_v4_top_amplifier", modeled in this document).
Construction recipe (the document's own serialized feature program — sketch geometry with constraints, then the solid features built on it; lengths are millimeters unless a unit is written):

FEATURE [PartDesign::SubShapeBinder] Binder153
  BindCopyOnChange = 0
  BindMode = 0
  ClaimChildren = true
  Context = -> Body150 [Binder153.]
  Fuse = false
  MakeFace = true
  OffsetFill = false
  OffsetIntersection = false
  OffsetJoinType = 0
  OffsetOpenResult = false
  PartialLoad = false
  Relative = false
  Support = -> [Connect009]
  _Version = 2
FEATURE [PartDesign::Pad] Pad050
  Direction = (0,0,1)
  Length = 18
  Length2 = 10
  Profile = -> Binder153
  Suppressed = false
  Type = 0
FEATURE [PartDesign::Boolean] Boolean055
  BaseFeature = -> Pad050
  Group = -> [Compound109]
  Suppressed = false
  Type = 1
  UsePlacement = true
FEATURE [PartDesign::Body] Body150  label="basement_v4_top_amplifier"
  AllowCompound = false
  Group = -> [Binder153,Pad050,Boolean055]
  Origin = -> Origin131
  Tip = -> Boolean055
COMPONENT P31 — recipe-attached ("basement_v4_top", modeled in this document).
Construction recipe (the document's own serialized feature program — sketch geometry with constraints, then the solid features built on it; lengths are millimeters unless a unit is written):

FEATURE [PartDesign::SubShapeBinder] Binder152
  BindCopyOnChange = 0
  BindMode = 0
  ClaimChildren = true
  Context = -> Body151 [Binder152.]
  Fuse = true
  MakeFace = false
  OffsetFill = false
  OffsetIntersection = false
  OffsetJoinType = 0
  OffsetOpenResult = false
  PartialLoad = false
  Relative = false
  Support = -> [Connect010]
  _Version = 2
  expr: Support = <<Connect010>>._self
FEATURE [PartDesign::Pad] Pad049
  Direction = (0,0,1)
  Length = 18
  Length2 = 10
  Profile = -> Binder152
  Refine = true
  Suppressed = false
  Type = 0
FEATURE [Sketcher::SketchObject] Sketch277
  ArcFitTolerance = 0
  AttachmentOffset = pos=(-253,0,0) rot=(0,0,1;0rad)
  AttachmentSupport = -> [YZ_Plane131]
  FullyConstrained = true
  MakeInternals = false
  MapMode = 5
  Placement = pos=(0,-253,0) rot=(0.57735,0.57735,0.57735;2.0944rad)
  sketch-geometry (3):
    g0: LineSegment StartX=0 StartY=15 StartZ=0 EndX=0 EndY=0 EndZ=0
    g1: LineSegment StartX=0 StartY=0 StartZ=0 EndX=15 EndY=0 EndZ=0
    g2: LineSegment StartX=15 StartY=0 StartZ=0 EndX=0 EndY=15 EndZ=0
  constraints (8):
    c: PointOnObject(g0,g-2)
    c: Coincident(g0,g-1)
    c: Coincident(g0,g1)
    c: PointOnObject(g1,g-1)
    c: Coincident(g1,g2)
    c: Coincident(g2,g0)
    c: Angle(g2) = 2.35619
    c: DistanceY(g0,g0) = 15
FEATURE [PartDesign::SubtractivePipe] SubtractivePipe001
  AuxilleryCurvelinear = true
  AuxillerySpineTangent = false
  BaseFeature = -> Pad049
  Binormal = (0,0,0)
  Mode = 0
  Profile = -> Sketch277
  Spine = -> Binder152 [Edge14,Edge13,Edge12,Edge11,Edge10,Edge9,Edge8,Edge7,Edge6,Edge5,Edge4,Edge3,Edge2,Edge1,Edge18,Edge17,Edge16,Edge15]
  SpineTangent = false
  Suppressed = false
  Transformation = 0
  Transition = 0
FEATURE [PartDesign::Boolean] Boolean056
  BaseFeature = -> SubtractivePipe001
  Group = -> [Compound110]
  Refine = true
  Suppressed = false
  Type = 1
  UsePlacement = true
FEATURE [PartDesign::Body] Body151  label="basement_v4_top"
  AllowCompound = false
  Group = -> [Binder152,Pad049,SubtractivePipe001,Boolean056,Sketch277]
  Origin = -> Origin132
  Tip = -> SubtractivePipe001
COMPONENT P32 — recipe-attached ("pillar3_plexiglass_outer", modeled in this document).
Construction recipe (the document's own serialized feature program — sketch geometry with constraints, then the solid features built on it; lengths are millimeters unless a unit is written):

FEATURE [PartDesign::SubShapeBinder] Binder154
  BindCopyOnChange = 0
  BindMode = 0
  ClaimChildren = true
  Context = -> Body152 [Binder154.]
  Fuse = false
  MakeFace = true
  OffsetFill = false
  OffsetIntersection = false
  OffsetJoinType = 0
  OffsetOpenResult = false
  PartialLoad = false
  Relative = true
  Support = -> [Connect012]
  _Version = 2
FEATURE [PartDesign::FeaturePython] BaseBend057  # WARN: FeaturePython — macro-defined, semantics opaque (R4)
  BendSide = 1
  BendSketch = -> Binder154
  MidPlane = false
  Reverse = false
  Suppressed = false
  length = 1214
  radius = 1
  thickness = 1.5
FEATURE [PartDesign::Boolean] Boolean057
  BaseFeature = -> BaseBend057
  Group = -> [Compound113]
  Refine = true
  Suppressed = false
  Type = 1
  UsePlacement = true
FEATURE [PartDesign::CoordinateSystem] Local_CS049
  AttacherType = Attacher::AttachEngine3D
  AttachmentSupport = -> [XY_Plane132]
  MapMode = 5
FEATURE [PartDesign::Body] Body152  label="pillar3_plexiglass_outer"
  AllowCompound = false
  Group = -> [Binder154,BaseBend057,Boolean057,Local_CS049]
  Origin = -> Origin133
  Tip = -> Boolean057
COMPONENT P33 — recipe-attached ("Body153", modeled in this document).
Construction recipe (the document's own serialized feature program — sketch geometry with constraints, then the solid features built on it; lengths are millimeters unless a unit is written):

FEATURE [Sketcher::SketchObject] Sketch282
  ArcFitTolerance = 0
  AttachmentSupport = -> [XY_Plane133]
  FullyConstrained = true
  MakeInternals = false
  MapMode = 5
  sketch-geometry (7):
    g0: LineSegment StartX=10.9697 StartY=0 StartZ=0 EndX=5.48483 EndY=9.5 EndZ=0
    g1: LineSegment StartX=5.48483 StartY=9.5 StartZ=0 EndX=-5.48483 EndY=9.5 EndZ=0
    g2: LineSegment StartX=-5.48483 StartY=9.5 StartZ=0 EndX=-10.9697 EndY=0 EndZ=0
    g3: LineSegment StartX=-10.9697 StartY=7e-16 StartZ=0 EndX=-5.48483 EndY=-9.5 EndZ=0
    g4: LineSegment StartX=-5.48483 StartY=-9.5 StartZ=0 EndX=5.48483 EndY=-9.5 EndZ=0
    g5: LineSegment StartX=5.48483 StartY=-9.5 StartZ=0 EndX=10.9697 EndY=0 EndZ=0
    g6: Circle [constr] CenterX=0 CenterY=0 CenterZ=0 NormalX=0 NormalY=0 NormalZ=1 AngleXU=0 Radius=10.9697
  constraints (16):
    c: Coincident(g0,g1)
    c: Coincident(g1,g2)
    c: Coincident(g2,g3)
    c: Coincident(g3,g4)
    c: Coincident(g4,g5)
    c: Coincident(g5,g0)
    c: Equal(g0, g1-g5) x5
    c: PointOnObject(g0,g6)
    c: PointOnObject(g1,g6)
    c: PointOnObject(g2,g6)
    c: PointOnObject(g3,g6)
    c: PointOnObject(g4,g6)
    c: PointOnObject(g5,g6)
    c: Coincident(g6,g-1)
    c: PointOnObject(g5,g-1)
    c: DistanceY(g4,g0) = 19
FEATURE [PartDesign::Pad] Pad051
  Direction = (0,0,1)
  Length = 7
  Length2 = 10
  Profile = -> Sketch282
  ReferenceAxis = -> Sketch282 [N_Axis]
  Suppressed = false
  Type = 0
FEATURE [PartDesign::AdditiveCylinder] Cylinder016
  Angle = 360
  AttacherType = Attacher::AttachEngine3D
  BaseFeature = -> Pad051
  FirstAngle = 0
  Height = 40
  Radius = 6
  SecondAngle = 0
  Suppressed = false
FEATURE [PartDesign::Body] Body153
  AllowCompound = false
  Group = -> [Sketch282,Pad051,Cylinder016]
  Origin = -> Origin134
  Tip = -> Cylinder016
COMPONENT P34 — recipe-attached ("Body154", modeled in this document).
Construction recipe (the document's own serialized feature program — sketch geometry with constraints, then the solid features built on it; lengths are millimeters unless a unit is written):

FEATURE [Sketcher::SketchObject] Sketch283
  ArcFitTolerance = 0
  AttachmentSupport = -> [XZ_Plane134]
  FullyConstrained = true
  MakeInternals = false
  MapMode = 5
  Placement = pos=(0,0,0) rot=(1,0,0;1.5708rad)
  sketch-geometry (6):
    g0: LineSegment StartX=9 StartY=0 StartZ=0 EndX=19.35 EndY=0 EndZ=0
    g1: LineSegment StartX=19.35 StartY=0 StartZ=0 EndX=20.35 EndY=7 EndZ=0
    g2: LineSegment StartX=20.35 StartY=7 StartZ=0 EndX=18.15 EndY=22.25 EndZ=0
    g3: LineSegment StartX=18.15 StartY=22.25 StartZ=0 EndX=18.15 EndY=25.5 EndZ=0
    g4: LineSegment StartX=18.15 StartY=25.5 StartZ=0 EndX=9 EndY=25.5 EndZ=0
    g5: LineSegment StartX=9 StartY=25.5 StartZ=0 EndX=9 EndY=0 EndZ=0
  constraints (18):
    c: PointOnObject(g0,g-1)
    c: PointOnObject(g0,g-1)
    c: Coincident(g0,g1)
    c: Coincident(g1,g2)
    c: Coincident(g2,g3)
    c: Vertical(g3)
    c: Coincident(g3,g4)
    c: Horizontal(g4)
    c: Coincident(g4,g5)
    c: Coincident(g5,g0)
    c: Vertical(g5)
    c: DistanceX(g0) = 9
    c: DistanceY(g4) = 25.5
    c: DistanceX(g0) = 19.35
    c: DistanceX(g3) = 18.15
    c: DistanceY(g1) = 7
    c: DistanceY(g3,g3) = 3.25
    c: DistanceX(g1) = 20.35
FEATURE [PartDesign::Revolution] Revolution007
  Angle = 360
  Angle2 = 60
  Axis = (0,2e-16,1)
  Base = (0,0,0)
  Placement = pos=(0,0,0) rot=(1,0,0;1.5708rad)
  Profile = -> Sketch283
  ReferenceAxis = -> Sketch283 [V_Axis]
  Reversed = true
  Suppressed = false
  Type = 0
FEATURE [PartDesign::Plane] DatumPlane010
  AttachmentOffset = pos=(0,0,25.5) rot=(0,0,1;0rad)
  AttachmentSupport = -> [XY_Plane134]
  Length = 60
  MapMode = 5
  Placement = pos=(0,0,25.5) rot=(0,0,1;0rad)
  ResizeMode = 0
  Width = 60
FEATURE [PartDesign::Mirrored] Mirrored025
  BaseFeature = -> Revolution007
  MirrorPlane = -> DatumPlane010
  Originals = -> [Revolution007]
  Placement = pos=(0,0,0) rot=(1,0,0;1.5708rad)
  Refine = true
  Suppressed = false
  TransformMode = 0
FEATURE [PartDesign::Body] Body154
  AllowCompound = false
  Group = -> [Sketch283,Revolution007,DatumPlane010,Mirrored025]
  Origin = -> Origin135
  Tip = -> Mirrored025
COMPONENT P35 — recipe-attached ("Body155", modeled in this document).
Construction recipe (the document's own serialized feature program — sketch geometry with constraints, then the solid features built on it; lengths are millimeters unless a unit is written):

FEATURE [Sketcher::SketchObject] Sketch286
  ArcFitTolerance = 0
  AttachmentOffset = pos=(0,0,512) rot=(0,0,1;0rad)
  AttachmentSupport = -> [XY_Plane135]
  FullyConstrained = true
  MakeInternals = false
  MapMode = 5
  Placement = pos=(0,0,512) rot=(0,0,1;0rad)
  sketch-geometry (8):
    g0: LineSegment [constr] StartX=0 StartY=0 StartZ=0 EndX=14.5 EndY=8.37158 EndZ=0
    g1: LineSegment [constr] StartX=14.5 StartY=8.37158 StartZ=0 EndX=14.5 EndY=4.90748 EndZ=0
    g2: LineSegment [constr] StartX=14.5 StartY=4.90748 StartZ=0 EndX=29.6554 EndY=-3.84252 EndZ=0
    g3: LineSegment StartX=28.1554 StartY=-6.4406 StartZ=0 EndX=11.5 EndY=3.17543 EndZ=0
    g4: LineSegment StartX=11.5 StartY=3.17543 StartZ=0 EndX=11.5 EndY=22.4075 EndZ=0
    g5: LineSegment [constr] StartX=14.5 StartY=4.90748 StartZ=0 EndX=11.5 EndY=4.90748 EndZ=0
    g6: LineSegment [constr] StartX=14.5 StartY=4.90748 StartZ=0 EndX=13 EndY=2.3094 EndZ=0
    g7: LineSegment [constr] StartX=28.1554 StartY=-6.4406 StartZ=0 EndX=29.6554 EndY=-3.84252 EndZ=0
  constraints (24):
    c: Coincident(g-1,g0)
    c: DistanceX(g0) = 14.5
    c: Angle(g0) = 0.523599
    c: Coincident(g0,g1)
    c: Vertical(g1)
    c: Coincident(g1,g2)
    c: Angle(g2) = -0.523599
    c: Distance(g0,g2) = 3
    c: Distance(g2) = 17.5
    c: Coincident(g3,g4)
    c: Vertical(g4)
    c: Parallel(g3,g2)
    c: Distance(g1,g4) = 3
    c: Coincident(g1,g5)
    c: PointOnObject(g5,g4)
    c: Horizontal(g5)
    c: Coincident(g1,g6)
    c: PointOnObject(g6,g3)
    c: Perpendicular(g3,g6)
    c: Equal(g6,g5)
    c: Equal(g3,g4)
    c: Coincident(g7,g2)
    c: Coincident(g7,g3)
    c: Perpendicular(g3,g7)
FEATURE [PartDesign::FeaturePython] BaseBend058  # WARN: FeaturePython — macro-defined, semantics opaque (R4)
  BendSide = 0
  BendSketch = -> Sketch286
  MidPlane = false
  Reverse = false
  Suppressed = false
  length = 842
  radius = 0.1
  thickness = 0.3
FEATURE [PartDesign::Boolean] Boolean059
  BaseFeature = -> BaseBend058
  Group = -> [Fusion006]
  Suppressed = false
  Type = 1
  UsePlacement = true
FEATURE [PartDesign::Body] Body155
  AllowCompound = false
  Group = -> [Sketch286,BaseBend058,Boolean059]
  Origin = -> Origin136
  Tip = -> Boolean059
COMPONENT P36 — geometry summary ("leg_amplifier_link"; no construction recipe available for this part):
  bounding box: 403.5 x 29.1 x 24.5 mm
  tessellated surface: 76 triangles
  volume: 6293 mm^3 (2% of its bounding box)
  symmetry: mirror-symmetric across its z mid-plane
